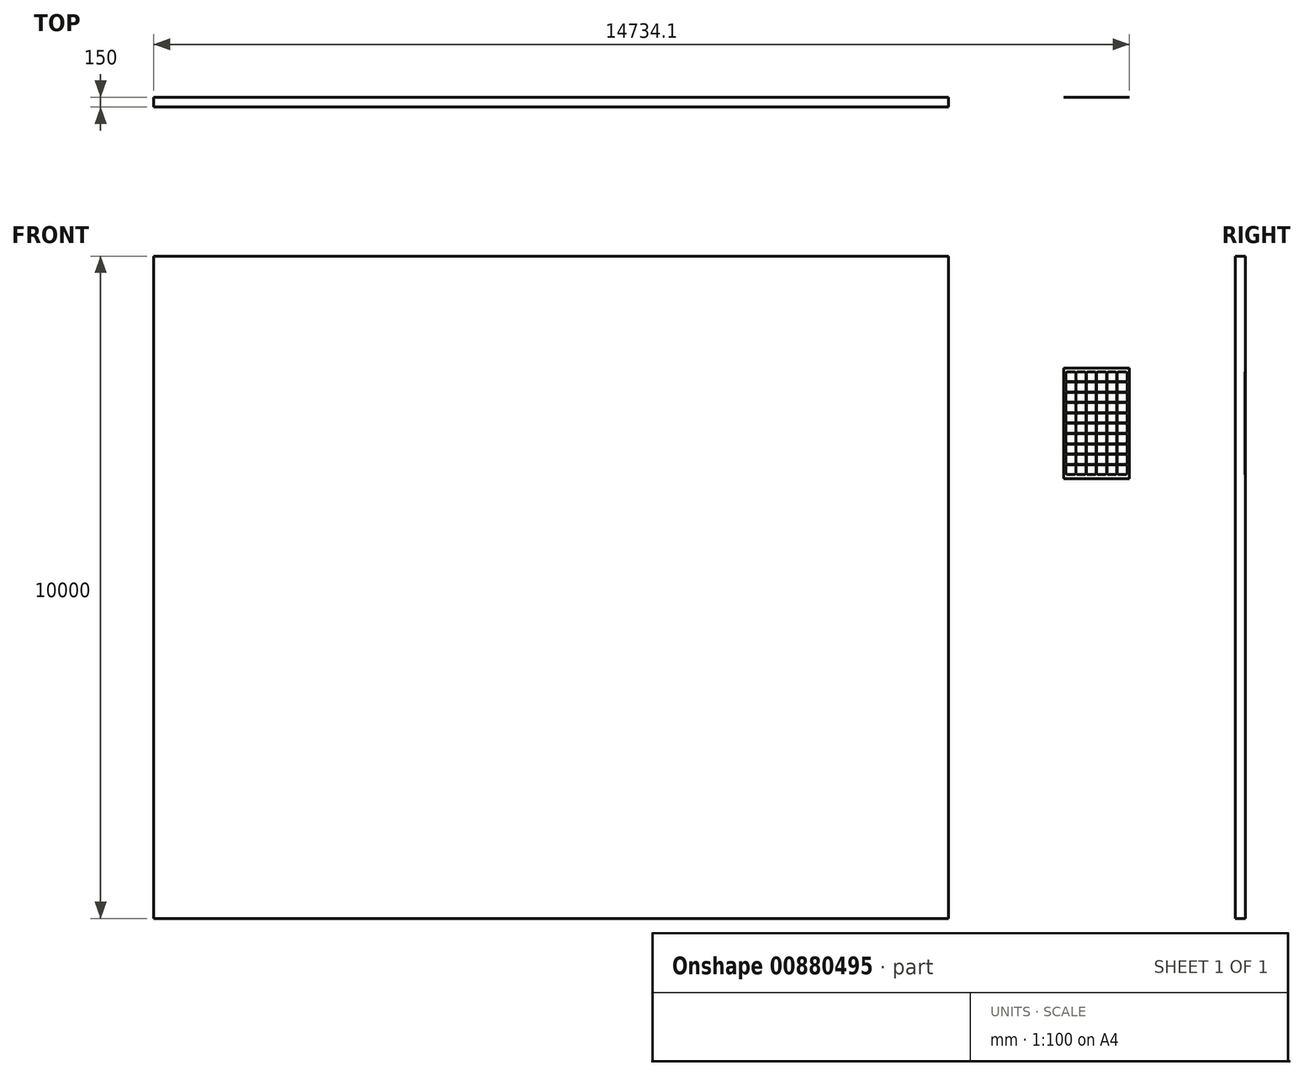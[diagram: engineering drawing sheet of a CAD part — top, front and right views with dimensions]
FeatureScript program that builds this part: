
annotation { "Feature Type Name" : "Feature", "Feature Type Description" : "" }
export const myFeature = defineFeature(function(context is Context, id is Id, definition is map)
    precondition{}
    {
        {
            var Q0;
            Q0=qCreatedBy(makeId("Front.planeOp"),FACE);
            var sketch = newSketch(context, id + "F0", { "sketchPlane" : qUnion([Q0])});
            skLineSegment(sketch, "E0.bottom", {"start": v(-6000, 5000) * mm, "end": v(6000, 5000) * mm});
            skLineSegment(sketch, "E0.top", {"start": v(-6000, -5000) * mm, "end": v(6000, -5000) * mm});
            skLineSegment(sketch, "E0.left", {"start": v(-6000, 5000) * mm, "end": v(-6000, -5000) * mm});
            skLineSegment(sketch, "E0.right", {"start": v(6000, 5000) * mm, "end": v(6000, -5000) * mm});
            skPoint(sketch, "E0.middle", {"position": v(0, 0) * mm});
            skSolve(sketch);
        }
        {
            var Q0;
            Q0=makeQuery(id+"F0.imprint","IMPRINT",FACE,{"disambiguationData":[TD([[makeQuery(id+"F0.imprint","IMPRINT",EDGE,{"derivedFrom":sQuery(id+"F0.wireOp",EDGE,"E0.bottom")}),-1.0]])]});
            var sketch = newSketch(context, id + "F1", { "sketchPlane" : qUnion([Q0])});
            skLineSegment(sketch, "E1.bottom", {"start": v(7744.06, 3311.69) * mm, "end": v(8734.06, 3311.69) * mm});
            skLineSegment(sketch, "E1.top", {"start": v(7744.06, 1636.69) * mm, "end": v(8734.06, 1636.69) * mm});
            skLineSegment(sketch, "E1.left", {"start": v(7744.06, 3311.69) * mm, "end": v(7744.06, 1636.69) * mm});
            skLineSegment(sketch, "E1.right", {"start": v(8734.06, 3311.69) * mm, "end": v(8734.06, 1636.69) * mm});
            skSolve(sketch);
        }
        {
            var Q0;
            Q0=makeQuery(id+"F1.imprint","IMPRINT",FACE,{"disambiguationData":[TD([[makeQuery(id+"F1.imprint","IMPRINT",EDGE,{"derivedFrom":sQuery(id+"F1.wireOp",EDGE,"E1.bottom")}),-1.0]])]});
            var sketch = newSketch(context, id + "F2", { "sketchPlane" : qUnion([Q0])});
            skLineSegment(sketch, "E2.bottom", {"start": v(7804.13, 1851.23) * mm, "end": v(7894.13, 1851.23) * mm});
            skLineSegment(sketch, "E2.top", {"start": v(7804.13, 1701.23) * mm, "end": v(7894.13, 1701.23) * mm});
            skLineSegment(sketch, "E2.left", {"start": v(7774.13, 1821.23) * mm, "end": v(7774.13, 1731.23) * mm});
            skLineSegment(sketch, "E2.right", {"start": v(7924.13, 1821.23) * mm, "end": v(7924.13, 1731.23) * mm});
            skPoint(sketch, "E3.visualSharp", {"position": v(7924.13, 1851.23) * mm});
            skArc(sketch, "E3.filletArc", {"start": v(7924.13, 1821.23) * mm, "mid": v(7915.35, 1842.44) * mm, "end": v(7894.13, 1851.23) * mm});
            skPoint(sketch, "E4.visualSharp", {"position": v(7774.13, 1851.23) * mm});
            skArc(sketch, "E4.filletArc", {"start": v(7804.13, 1851.23) * mm, "mid": v(7782.92, 1842.44) * mm, "end": v(7774.13, 1821.23) * mm});
            skPoint(sketch, "E5.visualSharp", {"position": v(7774.13, 1701.23) * mm});
            skArc(sketch, "E5.filletArc", {"start": v(7774.13, 1731.23) * mm, "mid": v(7782.92, 1710.01) * mm, "end": v(7804.13, 1701.23) * mm});
            skPoint(sketch, "E6.visualSharp", {"position": v(7924.13, 1701.23) * mm});
            skArc(sketch, "E6.filletArc", {"start": v(7894.13, 1701.23) * mm, "mid": v(7915.35, 1710.01) * mm, "end": v(7924.13, 1731.23) * mm});
            skLineSegment(sketch, "E7.0.1.0", {"start": v(7804.13, 2007.23) * mm, "end": v(7894.13, 2007.23) * mm});
            skArc(sketch, "E7.0.1.1", {"start": v(7804.13, 2007.23) * mm, "mid": v(7782.92, 1998.44) * mm, "end": v(7774.13, 1977.23) * mm});
            skLineSegment(sketch, "E7.0.1.2", {"start": v(7774.13, 1977.23) * mm, "end": v(7774.13, 1887.23) * mm});
            skLineSegment(sketch, "E7.0.1.3", {"start": v(7804.13, 1857.23) * mm, "end": v(7894.13, 1857.23) * mm});
            skArc(sketch, "E7.0.1.4", {"start": v(7774.13, 1887.23) * mm, "mid": v(7782.92, 1866.01) * mm, "end": v(7804.13, 1857.23) * mm});
            skArc(sketch, "E7.0.1.5", {"start": v(7894.13, 1857.23) * mm, "mid": v(7915.35, 1866.01) * mm, "end": v(7924.13, 1887.23) * mm});
            skLineSegment(sketch, "E7.0.1.6", {"start": v(7924.13, 1977.23) * mm, "end": v(7924.13, 1887.23) * mm});
            skArc(sketch, "E7.0.1.7", {"start": v(7924.13, 1977.23) * mm, "mid": v(7915.35, 1998.44) * mm, "end": v(7894.13, 2007.23) * mm});
            skLineSegment(sketch, "E7.0.2.0", {"start": v(7804.13, 2163.23) * mm, "end": v(7894.13, 2163.23) * mm});
            skArc(sketch, "E7.0.2.1", {"start": v(7804.13, 2163.23) * mm, "mid": v(7782.92, 2154.44) * mm, "end": v(7774.13, 2133.23) * mm});
            skLineSegment(sketch, "E7.0.2.2", {"start": v(7774.13, 2133.23) * mm, "end": v(7774.13, 2043.23) * mm});
            skLineSegment(sketch, "E7.0.2.3", {"start": v(7804.13, 2013.23) * mm, "end": v(7894.13, 2013.23) * mm});
            skArc(sketch, "E7.0.2.4", {"start": v(7774.13, 2043.23) * mm, "mid": v(7782.92, 2022.01) * mm, "end": v(7804.13, 2013.23) * mm});
            skArc(sketch, "E7.0.2.5", {"start": v(7894.13, 2013.23) * mm, "mid": v(7915.35, 2022.01) * mm, "end": v(7924.13, 2043.23) * mm});
            skLineSegment(sketch, "E7.0.2.6", {"start": v(7924.13, 2133.23) * mm, "end": v(7924.13, 2043.23) * mm});
            skArc(sketch, "E7.0.2.7", {"start": v(7924.13, 2133.23) * mm, "mid": v(7915.35, 2154.44) * mm, "end": v(7894.13, 2163.23) * mm});
            skLineSegment(sketch, "E7.0.3.0", {"start": v(7804.13, 2319.23) * mm, "end": v(7894.13, 2319.23) * mm});
            skArc(sketch, "E7.0.3.1", {"start": v(7804.13, 2319.23) * mm, "mid": v(7782.92, 2310.44) * mm, "end": v(7774.13, 2289.23) * mm});
            skLineSegment(sketch, "E7.0.3.2", {"start": v(7774.13, 2289.23) * mm, "end": v(7774.13, 2199.23) * mm});
            skLineSegment(sketch, "E7.0.3.3", {"start": v(7804.13, 2169.23) * mm, "end": v(7894.13, 2169.23) * mm});
            skArc(sketch, "E7.0.3.4", {"start": v(7774.13, 2199.23) * mm, "mid": v(7782.92, 2178.01) * mm, "end": v(7804.13, 2169.23) * mm});
            skArc(sketch, "E7.0.3.5", {"start": v(7894.13, 2169.23) * mm, "mid": v(7915.35, 2178.01) * mm, "end": v(7924.13, 2199.23) * mm});
            skLineSegment(sketch, "E7.0.3.6", {"start": v(7924.13, 2289.23) * mm, "end": v(7924.13, 2199.23) * mm});
            skArc(sketch, "E7.0.3.7", {"start": v(7924.13, 2289.23) * mm, "mid": v(7915.35, 2310.44) * mm, "end": v(7894.13, 2319.23) * mm});
            skLineSegment(sketch, "E7.0.4.0", {"start": v(7804.13, 2475.23) * mm, "end": v(7894.13, 2475.23) * mm});
            skArc(sketch, "E7.0.4.1", {"start": v(7804.13, 2475.23) * mm, "mid": v(7782.92, 2466.44) * mm, "end": v(7774.13, 2445.23) * mm});
            skLineSegment(sketch, "E7.0.4.2", {"start": v(7774.13, 2445.23) * mm, "end": v(7774.13, 2355.23) * mm});
            skLineSegment(sketch, "E7.0.4.3", {"start": v(7804.13, 2325.23) * mm, "end": v(7894.13, 2325.23) * mm});
            skArc(sketch, "E7.0.4.4", {"start": v(7774.13, 2355.23) * mm, "mid": v(7782.92, 2334.01) * mm, "end": v(7804.13, 2325.23) * mm});
            skArc(sketch, "E7.0.4.5", {"start": v(7894.13, 2325.23) * mm, "mid": v(7915.35, 2334.01) * mm, "end": v(7924.13, 2355.23) * mm});
            skLineSegment(sketch, "E7.0.4.6", {"start": v(7924.13, 2445.23) * mm, "end": v(7924.13, 2355.23) * mm});
            skArc(sketch, "E7.0.4.7", {"start": v(7924.13, 2445.23) * mm, "mid": v(7915.35, 2466.44) * mm, "end": v(7894.13, 2475.23) * mm});
            skLineSegment(sketch, "E7.0.5.0", {"start": v(7804.13, 2631.23) * mm, "end": v(7894.13, 2631.23) * mm});
            skArc(sketch, "E7.0.5.1", {"start": v(7804.13, 2631.23) * mm, "mid": v(7782.92, 2622.44) * mm, "end": v(7774.13, 2601.23) * mm});
            skLineSegment(sketch, "E7.0.5.2", {"start": v(7774.13, 2601.23) * mm, "end": v(7774.13, 2511.23) * mm});
            skLineSegment(sketch, "E7.0.5.3", {"start": v(7804.13, 2481.23) * mm, "end": v(7894.13, 2481.23) * mm});
            skArc(sketch, "E7.0.5.4", {"start": v(7774.13, 2511.23) * mm, "mid": v(7782.92, 2490.01) * mm, "end": v(7804.13, 2481.23) * mm});
            skArc(sketch, "E7.0.5.5", {"start": v(7894.13, 2481.23) * mm, "mid": v(7915.35, 2490.01) * mm, "end": v(7924.13, 2511.23) * mm});
            skLineSegment(sketch, "E7.0.5.6", {"start": v(7924.13, 2601.23) * mm, "end": v(7924.13, 2511.23) * mm});
            skArc(sketch, "E7.0.5.7", {"start": v(7924.13, 2601.23) * mm, "mid": v(7915.35, 2622.44) * mm, "end": v(7894.13, 2631.23) * mm});
            skLineSegment(sketch, "E7.0.6.0", {"start": v(7804.13, 2787.23) * mm, "end": v(7894.13, 2787.23) * mm});
            skArc(sketch, "E7.0.6.1", {"start": v(7804.13, 2787.23) * mm, "mid": v(7782.92, 2778.44) * mm, "end": v(7774.13, 2757.23) * mm});
            skLineSegment(sketch, "E7.0.6.2", {"start": v(7774.13, 2757.23) * mm, "end": v(7774.13, 2667.23) * mm});
            skLineSegment(sketch, "E7.0.6.3", {"start": v(7804.13, 2637.23) * mm, "end": v(7894.13, 2637.23) * mm});
            skArc(sketch, "E7.0.6.4", {"start": v(7774.13, 2667.23) * mm, "mid": v(7782.92, 2646.01) * mm, "end": v(7804.13, 2637.23) * mm});
            skArc(sketch, "E7.0.6.5", {"start": v(7894.13, 2637.23) * mm, "mid": v(7915.35, 2646.01) * mm, "end": v(7924.13, 2667.23) * mm});
            skLineSegment(sketch, "E7.0.6.6", {"start": v(7924.13, 2757.23) * mm, "end": v(7924.13, 2667.23) * mm});
            skArc(sketch, "E7.0.6.7", {"start": v(7924.13, 2757.23) * mm, "mid": v(7915.35, 2778.44) * mm, "end": v(7894.13, 2787.23) * mm});
            skLineSegment(sketch, "E7.0.7.0", {"start": v(7804.13, 2943.23) * mm, "end": v(7894.13, 2943.23) * mm});
            skArc(sketch, "E7.0.7.1", {"start": v(7804.13, 2943.23) * mm, "mid": v(7782.92, 2934.44) * mm, "end": v(7774.13, 2913.23) * mm});
            skLineSegment(sketch, "E7.0.7.2", {"start": v(7774.13, 2913.23) * mm, "end": v(7774.13, 2823.23) * mm});
            skLineSegment(sketch, "E7.0.7.3", {"start": v(7804.13, 2793.23) * mm, "end": v(7894.13, 2793.23) * mm});
            skArc(sketch, "E7.0.7.4", {"start": v(7774.13, 2823.23) * mm, "mid": v(7782.92, 2802.01) * mm, "end": v(7804.13, 2793.23) * mm});
            skArc(sketch, "E7.0.7.5", {"start": v(7894.13, 2793.23) * mm, "mid": v(7915.35, 2802.01) * mm, "end": v(7924.13, 2823.23) * mm});
            skLineSegment(sketch, "E7.0.7.6", {"start": v(7924.13, 2913.23) * mm, "end": v(7924.13, 2823.23) * mm});
            skArc(sketch, "E7.0.7.7", {"start": v(7924.13, 2913.23) * mm, "mid": v(7915.35, 2934.44) * mm, "end": v(7894.13, 2943.23) * mm});
            skLineSegment(sketch, "E7.0.8.0", {"start": v(7804.13, 3099.23) * mm, "end": v(7894.13, 3099.23) * mm});
            skArc(sketch, "E7.0.8.1", {"start": v(7804.13, 3099.23) * mm, "mid": v(7782.92, 3090.44) * mm, "end": v(7774.13, 3069.23) * mm});
            skLineSegment(sketch, "E7.0.8.2", {"start": v(7774.13, 3069.23) * mm, "end": v(7774.13, 2979.23) * mm});
            skLineSegment(sketch, "E7.0.8.3", {"start": v(7804.13, 2949.23) * mm, "end": v(7894.13, 2949.23) * mm});
            skArc(sketch, "E7.0.8.4", {"start": v(7774.13, 2979.23) * mm, "mid": v(7782.92, 2958.01) * mm, "end": v(7804.13, 2949.23) * mm});
            skArc(sketch, "E7.0.8.5", {"start": v(7894.13, 2949.23) * mm, "mid": v(7915.35, 2958.01) * mm, "end": v(7924.13, 2979.23) * mm});
            skLineSegment(sketch, "E7.0.8.6", {"start": v(7924.13, 3069.23) * mm, "end": v(7924.13, 2979.23) * mm});
            skArc(sketch, "E7.0.8.7", {"start": v(7924.13, 3069.23) * mm, "mid": v(7915.35, 3090.44) * mm, "end": v(7894.13, 3099.23) * mm});
            skLineSegment(sketch, "E7.0.9.0", {"start": v(7804.13, 3255.23) * mm, "end": v(7894.13, 3255.23) * mm});
            skArc(sketch, "E7.0.9.1", {"start": v(7804.13, 3255.23) * mm, "mid": v(7782.92, 3246.44) * mm, "end": v(7774.13, 3225.23) * mm});
            skLineSegment(sketch, "E7.0.9.2", {"start": v(7774.13, 3225.23) * mm, "end": v(7774.13, 3135.23) * mm});
            skLineSegment(sketch, "E7.0.9.3", {"start": v(7804.13, 3105.23) * mm, "end": v(7894.13, 3105.23) * mm});
            skArc(sketch, "E7.0.9.4", {"start": v(7774.13, 3135.23) * mm, "mid": v(7782.92, 3114.01) * mm, "end": v(7804.13, 3105.23) * mm});
            skArc(sketch, "E7.0.9.5", {"start": v(7894.13, 3105.23) * mm, "mid": v(7915.35, 3114.01) * mm, "end": v(7924.13, 3135.23) * mm});
            skLineSegment(sketch, "E7.0.9.6", {"start": v(7924.13, 3225.23) * mm, "end": v(7924.13, 3135.23) * mm});
            skArc(sketch, "E7.0.9.7", {"start": v(7924.13, 3225.23) * mm, "mid": v(7915.35, 3246.44) * mm, "end": v(7894.13, 3255.23) * mm});
            skLineSegment(sketch, "E7.1.0.0", {"start": v(7959.13, 1851.23) * mm, "end": v(8049.13, 1851.23) * mm});
            skArc(sketch, "E7.1.0.1", {"start": v(7959.13, 1851.23) * mm, "mid": v(7937.92, 1842.44) * mm, "end": v(7929.13, 1821.23) * mm});
            skLineSegment(sketch, "E7.1.0.2", {"start": v(7929.13, 1821.23) * mm, "end": v(7929.13, 1731.23) * mm});
            skLineSegment(sketch, "E7.1.0.3", {"start": v(7959.13, 1701.23) * mm, "end": v(8049.13, 1701.23) * mm});
            skArc(sketch, "E7.1.0.4", {"start": v(7929.13, 1731.23) * mm, "mid": v(7937.92, 1710.01) * mm, "end": v(7959.13, 1701.23) * mm});
            skArc(sketch, "E7.1.0.5", {"start": v(8049.13, 1701.23) * mm, "mid": v(8070.35, 1710.01) * mm, "end": v(8079.13, 1731.23) * mm});
            skLineSegment(sketch, "E7.1.0.6", {"start": v(8079.13, 1821.23) * mm, "end": v(8079.13, 1731.23) * mm});
            skArc(sketch, "E7.1.0.7", {"start": v(8079.13, 1821.23) * mm, "mid": v(8070.35, 1842.44) * mm, "end": v(8049.13, 1851.23) * mm});
            skLineSegment(sketch, "E7.1.1.0", {"start": v(7959.13, 2007.23) * mm, "end": v(8049.13, 2007.23) * mm});
            skArc(sketch, "E7.1.1.1", {"start": v(7959.13, 2007.23) * mm, "mid": v(7937.92, 1998.44) * mm, "end": v(7929.13, 1977.23) * mm});
            skLineSegment(sketch, "E7.1.1.2", {"start": v(7929.13, 1977.23) * mm, "end": v(7929.13, 1887.23) * mm});
            skLineSegment(sketch, "E7.1.1.3", {"start": v(7959.13, 1857.23) * mm, "end": v(8049.13, 1857.23) * mm});
            skArc(sketch, "E7.1.1.4", {"start": v(7929.13, 1887.23) * mm, "mid": v(7937.92, 1866.01) * mm, "end": v(7959.13, 1857.23) * mm});
            skArc(sketch, "E7.1.1.5", {"start": v(8049.13, 1857.23) * mm, "mid": v(8070.35, 1866.01) * mm, "end": v(8079.13, 1887.23) * mm});
            skLineSegment(sketch, "E7.1.1.6", {"start": v(8079.13, 1977.23) * mm, "end": v(8079.13, 1887.23) * mm});
            skArc(sketch, "E7.1.1.7", {"start": v(8079.13, 1977.23) * mm, "mid": v(8070.35, 1998.44) * mm, "end": v(8049.13, 2007.23) * mm});
            skLineSegment(sketch, "E7.1.2.0", {"start": v(7959.13, 2163.23) * mm, "end": v(8049.13, 2163.23) * mm});
            skArc(sketch, "E7.1.2.1", {"start": v(7959.13, 2163.23) * mm, "mid": v(7937.92, 2154.44) * mm, "end": v(7929.13, 2133.23) * mm});
            skLineSegment(sketch, "E7.1.2.2", {"start": v(7929.13, 2133.23) * mm, "end": v(7929.13, 2043.23) * mm});
            skLineSegment(sketch, "E7.1.2.3", {"start": v(7959.13, 2013.23) * mm, "end": v(8049.13, 2013.23) * mm});
            skArc(sketch, "E7.1.2.4", {"start": v(7929.13, 2043.23) * mm, "mid": v(7937.92, 2022.01) * mm, "end": v(7959.13, 2013.23) * mm});
            skArc(sketch, "E7.1.2.5", {"start": v(8049.13, 2013.23) * mm, "mid": v(8070.35, 2022.01) * mm, "end": v(8079.13, 2043.23) * mm});
            skLineSegment(sketch, "E7.1.2.6", {"start": v(8079.13, 2133.23) * mm, "end": v(8079.13, 2043.23) * mm});
            skArc(sketch, "E7.1.2.7", {"start": v(8079.13, 2133.23) * mm, "mid": v(8070.35, 2154.44) * mm, "end": v(8049.13, 2163.23) * mm});
            skLineSegment(sketch, "E7.1.3.0", {"start": v(7959.13, 2319.23) * mm, "end": v(8049.13, 2319.23) * mm});
            skArc(sketch, "E7.1.3.1", {"start": v(7959.13, 2319.23) * mm, "mid": v(7937.92, 2310.44) * mm, "end": v(7929.13, 2289.23) * mm});
            skLineSegment(sketch, "E7.1.3.2", {"start": v(7929.13, 2289.23) * mm, "end": v(7929.13, 2199.23) * mm});
            skLineSegment(sketch, "E7.1.3.3", {"start": v(7959.13, 2169.23) * mm, "end": v(8049.13, 2169.23) * mm});
            skArc(sketch, "E7.1.3.4", {"start": v(7929.13, 2199.23) * mm, "mid": v(7937.92, 2178.01) * mm, "end": v(7959.13, 2169.23) * mm});
            skArc(sketch, "E7.1.3.5", {"start": v(8049.13, 2169.23) * mm, "mid": v(8070.35, 2178.01) * mm, "end": v(8079.13, 2199.23) * mm});
            skLineSegment(sketch, "E7.1.3.6", {"start": v(8079.13, 2289.23) * mm, "end": v(8079.13, 2199.23) * mm});
            skArc(sketch, "E7.1.3.7", {"start": v(8079.13, 2289.23) * mm, "mid": v(8070.35, 2310.44) * mm, "end": v(8049.13, 2319.23) * mm});
            skLineSegment(sketch, "E7.1.4.0", {"start": v(7959.13, 2475.23) * mm, "end": v(8049.13, 2475.23) * mm});
            skArc(sketch, "E7.1.4.1", {"start": v(7959.13, 2475.23) * mm, "mid": v(7937.92, 2466.44) * mm, "end": v(7929.13, 2445.23) * mm});
            skLineSegment(sketch, "E7.1.4.2", {"start": v(7929.13, 2445.23) * mm, "end": v(7929.13, 2355.23) * mm});
            skLineSegment(sketch, "E7.1.4.3", {"start": v(7959.13, 2325.23) * mm, "end": v(8049.13, 2325.23) * mm});
            skArc(sketch, "E7.1.4.4", {"start": v(7929.13, 2355.23) * mm, "mid": v(7937.92, 2334.01) * mm, "end": v(7959.13, 2325.23) * mm});
            skArc(sketch, "E7.1.4.5", {"start": v(8049.13, 2325.23) * mm, "mid": v(8070.35, 2334.01) * mm, "end": v(8079.13, 2355.23) * mm});
            skLineSegment(sketch, "E7.1.4.6", {"start": v(8079.13, 2445.23) * mm, "end": v(8079.13, 2355.23) * mm});
            skArc(sketch, "E7.1.4.7", {"start": v(8079.13, 2445.23) * mm, "mid": v(8070.35, 2466.44) * mm, "end": v(8049.13, 2475.23) * mm});
            skLineSegment(sketch, "E7.1.5.0", {"start": v(7959.13, 2631.23) * mm, "end": v(8049.13, 2631.23) * mm});
            skArc(sketch, "E7.1.5.1", {"start": v(7959.13, 2631.23) * mm, "mid": v(7937.92, 2622.44) * mm, "end": v(7929.13, 2601.23) * mm});
            skLineSegment(sketch, "E7.1.5.2", {"start": v(7929.13, 2601.23) * mm, "end": v(7929.13, 2511.23) * mm});
            skLineSegment(sketch, "E7.1.5.3", {"start": v(7959.13, 2481.23) * mm, "end": v(8049.13, 2481.23) * mm});
            skArc(sketch, "E7.1.5.4", {"start": v(7929.13, 2511.23) * mm, "mid": v(7937.92, 2490.01) * mm, "end": v(7959.13, 2481.23) * mm});
            skArc(sketch, "E7.1.5.5", {"start": v(8049.13, 2481.23) * mm, "mid": v(8070.35, 2490.01) * mm, "end": v(8079.13, 2511.23) * mm});
            skLineSegment(sketch, "E7.1.5.6", {"start": v(8079.13, 2601.23) * mm, "end": v(8079.13, 2511.23) * mm});
            skArc(sketch, "E7.1.5.7", {"start": v(8079.13, 2601.23) * mm, "mid": v(8070.35, 2622.44) * mm, "end": v(8049.13, 2631.23) * mm});
            skLineSegment(sketch, "E7.1.6.0", {"start": v(7959.13, 2787.23) * mm, "end": v(8049.13, 2787.23) * mm});
            skArc(sketch, "E7.1.6.1", {"start": v(7959.13, 2787.23) * mm, "mid": v(7937.92, 2778.44) * mm, "end": v(7929.13, 2757.23) * mm});
            skLineSegment(sketch, "E7.1.6.2", {"start": v(7929.13, 2757.23) * mm, "end": v(7929.13, 2667.23) * mm});
            skLineSegment(sketch, "E7.1.6.3", {"start": v(7959.13, 2637.23) * mm, "end": v(8049.13, 2637.23) * mm});
            skArc(sketch, "E7.1.6.4", {"start": v(7929.13, 2667.23) * mm, "mid": v(7937.92, 2646.01) * mm, "end": v(7959.13, 2637.23) * mm});
            skArc(sketch, "E7.1.6.5", {"start": v(8049.13, 2637.23) * mm, "mid": v(8070.35, 2646.01) * mm, "end": v(8079.13, 2667.23) * mm});
            skLineSegment(sketch, "E7.1.6.6", {"start": v(8079.13, 2757.23) * mm, "end": v(8079.13, 2667.23) * mm});
            skArc(sketch, "E7.1.6.7", {"start": v(8079.13, 2757.23) * mm, "mid": v(8070.35, 2778.44) * mm, "end": v(8049.13, 2787.23) * mm});
            skLineSegment(sketch, "E7.1.7.0", {"start": v(7959.13, 2943.23) * mm, "end": v(8049.13, 2943.23) * mm});
            skArc(sketch, "E7.1.7.1", {"start": v(7959.13, 2943.23) * mm, "mid": v(7937.92, 2934.44) * mm, "end": v(7929.13, 2913.23) * mm});
            skLineSegment(sketch, "E7.1.7.2", {"start": v(7929.13, 2913.23) * mm, "end": v(7929.13, 2823.23) * mm});
            skLineSegment(sketch, "E7.1.7.3", {"start": v(7959.13, 2793.23) * mm, "end": v(8049.13, 2793.23) * mm});
            skArc(sketch, "E7.1.7.4", {"start": v(7929.13, 2823.23) * mm, "mid": v(7937.92, 2802.01) * mm, "end": v(7959.13, 2793.23) * mm});
            skArc(sketch, "E7.1.7.5", {"start": v(8049.13, 2793.23) * mm, "mid": v(8070.35, 2802.01) * mm, "end": v(8079.13, 2823.23) * mm});
            skLineSegment(sketch, "E7.1.7.6", {"start": v(8079.13, 2913.23) * mm, "end": v(8079.13, 2823.23) * mm});
            skArc(sketch, "E7.1.7.7", {"start": v(8079.13, 2913.23) * mm, "mid": v(8070.35, 2934.44) * mm, "end": v(8049.13, 2943.23) * mm});
            skLineSegment(sketch, "E7.1.8.0", {"start": v(7959.13, 3099.23) * mm, "end": v(8049.13, 3099.23) * mm});
            skArc(sketch, "E7.1.8.1", {"start": v(7959.13, 3099.23) * mm, "mid": v(7937.92, 3090.44) * mm, "end": v(7929.13, 3069.23) * mm});
            skLineSegment(sketch, "E7.1.8.2", {"start": v(7929.13, 3069.23) * mm, "end": v(7929.13, 2979.23) * mm});
            skLineSegment(sketch, "E7.1.8.3", {"start": v(7959.13, 2949.23) * mm, "end": v(8049.13, 2949.23) * mm});
            skArc(sketch, "E7.1.8.4", {"start": v(7929.13, 2979.23) * mm, "mid": v(7937.92, 2958.01) * mm, "end": v(7959.13, 2949.23) * mm});
            skArc(sketch, "E7.1.8.5", {"start": v(8049.13, 2949.23) * mm, "mid": v(8070.35, 2958.01) * mm, "end": v(8079.13, 2979.23) * mm});
            skLineSegment(sketch, "E7.1.8.6", {"start": v(8079.13, 3069.23) * mm, "end": v(8079.13, 2979.23) * mm});
            skArc(sketch, "E7.1.8.7", {"start": v(8079.13, 3069.23) * mm, "mid": v(8070.35, 3090.44) * mm, "end": v(8049.13, 3099.23) * mm});
            skLineSegment(sketch, "E7.1.9.0", {"start": v(7959.13, 3255.23) * mm, "end": v(8049.13, 3255.23) * mm});
            skArc(sketch, "E7.1.9.1", {"start": v(7959.13, 3255.23) * mm, "mid": v(7937.92, 3246.44) * mm, "end": v(7929.13, 3225.23) * mm});
            skLineSegment(sketch, "E7.1.9.2", {"start": v(7929.13, 3225.23) * mm, "end": v(7929.13, 3135.23) * mm});
            skLineSegment(sketch, "E7.1.9.3", {"start": v(7959.13, 3105.23) * mm, "end": v(8049.13, 3105.23) * mm});
            skArc(sketch, "E7.1.9.4", {"start": v(7929.13, 3135.23) * mm, "mid": v(7937.92, 3114.01) * mm, "end": v(7959.13, 3105.23) * mm});
            skArc(sketch, "E7.1.9.5", {"start": v(8049.13, 3105.23) * mm, "mid": v(8070.35, 3114.01) * mm, "end": v(8079.13, 3135.23) * mm});
            skLineSegment(sketch, "E7.1.9.6", {"start": v(8079.13, 3225.23) * mm, "end": v(8079.13, 3135.23) * mm});
            skArc(sketch, "E7.1.9.7", {"start": v(8079.13, 3225.23) * mm, "mid": v(8070.35, 3246.44) * mm, "end": v(8049.13, 3255.23) * mm});
            skLineSegment(sketch, "E7.2.0.0", {"start": v(8114.13, 1851.23) * mm, "end": v(8204.13, 1851.23) * mm});
            skArc(sketch, "E7.2.0.1", {"start": v(8114.13, 1851.23) * mm, "mid": v(8092.92, 1842.44) * mm, "end": v(8084.13, 1821.23) * mm});
            skLineSegment(sketch, "E7.2.0.2", {"start": v(8084.13, 1821.23) * mm, "end": v(8084.13, 1731.23) * mm});
            skLineSegment(sketch, "E7.2.0.3", {"start": v(8114.13, 1701.23) * mm, "end": v(8204.13, 1701.23) * mm});
            skArc(sketch, "E7.2.0.4", {"start": v(8084.13, 1731.23) * mm, "mid": v(8092.92, 1710.01) * mm, "end": v(8114.13, 1701.23) * mm});
            skArc(sketch, "E7.2.0.5", {"start": v(8204.13, 1701.23) * mm, "mid": v(8225.35, 1710.01) * mm, "end": v(8234.13, 1731.23) * mm});
            skLineSegment(sketch, "E7.2.0.6", {"start": v(8234.13, 1821.23) * mm, "end": v(8234.13, 1731.23) * mm});
            skArc(sketch, "E7.2.0.7", {"start": v(8234.13, 1821.23) * mm, "mid": v(8225.35, 1842.44) * mm, "end": v(8204.13, 1851.23) * mm});
            skLineSegment(sketch, "E7.2.1.0", {"start": v(8114.13, 2007.23) * mm, "end": v(8204.13, 2007.23) * mm});
            skArc(sketch, "E7.2.1.1", {"start": v(8114.13, 2007.23) * mm, "mid": v(8092.92, 1998.44) * mm, "end": v(8084.13, 1977.23) * mm});
            skLineSegment(sketch, "E7.2.1.2", {"start": v(8084.13, 1977.23) * mm, "end": v(8084.13, 1887.23) * mm});
            skLineSegment(sketch, "E7.2.1.3", {"start": v(8114.13, 1857.23) * mm, "end": v(8204.13, 1857.23) * mm});
            skArc(sketch, "E7.2.1.4", {"start": v(8084.13, 1887.23) * mm, "mid": v(8092.92, 1866.01) * mm, "end": v(8114.13, 1857.23) * mm});
            skArc(sketch, "E7.2.1.5", {"start": v(8204.13, 1857.23) * mm, "mid": v(8225.35, 1866.01) * mm, "end": v(8234.13, 1887.23) * mm});
            skLineSegment(sketch, "E7.2.1.6", {"start": v(8234.13, 1977.23) * mm, "end": v(8234.13, 1887.23) * mm});
            skArc(sketch, "E7.2.1.7", {"start": v(8234.13, 1977.23) * mm, "mid": v(8225.35, 1998.44) * mm, "end": v(8204.13, 2007.23) * mm});
            skLineSegment(sketch, "E7.2.2.0", {"start": v(8114.13, 2163.23) * mm, "end": v(8204.13, 2163.23) * mm});
            skArc(sketch, "E7.2.2.1", {"start": v(8114.13, 2163.23) * mm, "mid": v(8092.92, 2154.44) * mm, "end": v(8084.13, 2133.23) * mm});
            skLineSegment(sketch, "E7.2.2.2", {"start": v(8084.13, 2133.23) * mm, "end": v(8084.13, 2043.23) * mm});
            skLineSegment(sketch, "E7.2.2.3", {"start": v(8114.13, 2013.23) * mm, "end": v(8204.13, 2013.23) * mm});
            skArc(sketch, "E7.2.2.4", {"start": v(8084.13, 2043.23) * mm, "mid": v(8092.92, 2022.01) * mm, "end": v(8114.13, 2013.23) * mm});
            skArc(sketch, "E7.2.2.5", {"start": v(8204.13, 2013.23) * mm, "mid": v(8225.35, 2022.01) * mm, "end": v(8234.13, 2043.23) * mm});
            skLineSegment(sketch, "E7.2.2.6", {"start": v(8234.13, 2133.23) * mm, "end": v(8234.13, 2043.23) * mm});
            skArc(sketch, "E7.2.2.7", {"start": v(8234.13, 2133.23) * mm, "mid": v(8225.35, 2154.44) * mm, "end": v(8204.13, 2163.23) * mm});
            skLineSegment(sketch, "E7.2.3.0", {"start": v(8114.13, 2319.23) * mm, "end": v(8204.13, 2319.23) * mm});
            skArc(sketch, "E7.2.3.1", {"start": v(8114.13, 2319.23) * mm, "mid": v(8092.92, 2310.44) * mm, "end": v(8084.13, 2289.23) * mm});
            skLineSegment(sketch, "E7.2.3.2", {"start": v(8084.13, 2289.23) * mm, "end": v(8084.13, 2199.23) * mm});
            skLineSegment(sketch, "E7.2.3.3", {"start": v(8114.13, 2169.23) * mm, "end": v(8204.13, 2169.23) * mm});
            skArc(sketch, "E7.2.3.4", {"start": v(8084.13, 2199.23) * mm, "mid": v(8092.92, 2178.01) * mm, "end": v(8114.13, 2169.23) * mm});
            skArc(sketch, "E7.2.3.5", {"start": v(8204.13, 2169.23) * mm, "mid": v(8225.35, 2178.01) * mm, "end": v(8234.13, 2199.23) * mm});
            skLineSegment(sketch, "E7.2.3.6", {"start": v(8234.13, 2289.23) * mm, "end": v(8234.13, 2199.23) * mm});
            skArc(sketch, "E7.2.3.7", {"start": v(8234.13, 2289.23) * mm, "mid": v(8225.35, 2310.44) * mm, "end": v(8204.13, 2319.23) * mm});
            skLineSegment(sketch, "E7.2.4.0", {"start": v(8114.13, 2475.23) * mm, "end": v(8204.13, 2475.23) * mm});
            skArc(sketch, "E7.2.4.1", {"start": v(8114.13, 2475.23) * mm, "mid": v(8092.92, 2466.44) * mm, "end": v(8084.13, 2445.23) * mm});
            skLineSegment(sketch, "E7.2.4.2", {"start": v(8084.13, 2445.23) * mm, "end": v(8084.13, 2355.23) * mm});
            skLineSegment(sketch, "E7.2.4.3", {"start": v(8114.13, 2325.23) * mm, "end": v(8204.13, 2325.23) * mm});
            skArc(sketch, "E7.2.4.4", {"start": v(8084.13, 2355.23) * mm, "mid": v(8092.92, 2334.01) * mm, "end": v(8114.13, 2325.23) * mm});
            skArc(sketch, "E7.2.4.5", {"start": v(8204.13, 2325.23) * mm, "mid": v(8225.35, 2334.01) * mm, "end": v(8234.13, 2355.23) * mm});
            skLineSegment(sketch, "E7.2.4.6", {"start": v(8234.13, 2445.23) * mm, "end": v(8234.13, 2355.23) * mm});
            skArc(sketch, "E7.2.4.7", {"start": v(8234.13, 2445.23) * mm, "mid": v(8225.35, 2466.44) * mm, "end": v(8204.13, 2475.23) * mm});
            skLineSegment(sketch, "E7.2.5.0", {"start": v(8114.13, 2631.23) * mm, "end": v(8204.13, 2631.23) * mm});
            skArc(sketch, "E7.2.5.1", {"start": v(8114.13, 2631.23) * mm, "mid": v(8092.92, 2622.44) * mm, "end": v(8084.13, 2601.23) * mm});
            skLineSegment(sketch, "E7.2.5.2", {"start": v(8084.13, 2601.23) * mm, "end": v(8084.13, 2511.23) * mm});
            skLineSegment(sketch, "E7.2.5.3", {"start": v(8114.13, 2481.23) * mm, "end": v(8204.13, 2481.23) * mm});
            skArc(sketch, "E7.2.5.4", {"start": v(8084.13, 2511.23) * mm, "mid": v(8092.92, 2490.01) * mm, "end": v(8114.13, 2481.23) * mm});
            skArc(sketch, "E7.2.5.5", {"start": v(8204.13, 2481.23) * mm, "mid": v(8225.35, 2490.01) * mm, "end": v(8234.13, 2511.23) * mm});
            skLineSegment(sketch, "E7.2.5.6", {"start": v(8234.13, 2601.23) * mm, "end": v(8234.13, 2511.23) * mm});
            skArc(sketch, "E7.2.5.7", {"start": v(8234.13, 2601.23) * mm, "mid": v(8225.35, 2622.44) * mm, "end": v(8204.13, 2631.23) * mm});
            skLineSegment(sketch, "E7.2.6.0", {"start": v(8114.13, 2787.23) * mm, "end": v(8204.13, 2787.23) * mm});
            skArc(sketch, "E7.2.6.1", {"start": v(8114.13, 2787.23) * mm, "mid": v(8092.92, 2778.44) * mm, "end": v(8084.13, 2757.23) * mm});
            skLineSegment(sketch, "E7.2.6.2", {"start": v(8084.13, 2757.23) * mm, "end": v(8084.13, 2667.23) * mm});
            skLineSegment(sketch, "E7.2.6.3", {"start": v(8114.13, 2637.23) * mm, "end": v(8204.13, 2637.23) * mm});
            skArc(sketch, "E7.2.6.4", {"start": v(8084.13, 2667.23) * mm, "mid": v(8092.92, 2646.01) * mm, "end": v(8114.13, 2637.23) * mm});
            skArc(sketch, "E7.2.6.5", {"start": v(8204.13, 2637.23) * mm, "mid": v(8225.35, 2646.01) * mm, "end": v(8234.13, 2667.23) * mm});
            skLineSegment(sketch, "E7.2.6.6", {"start": v(8234.13, 2757.23) * mm, "end": v(8234.13, 2667.23) * mm});
            skArc(sketch, "E7.2.6.7", {"start": v(8234.13, 2757.23) * mm, "mid": v(8225.35, 2778.44) * mm, "end": v(8204.13, 2787.23) * mm});
            skLineSegment(sketch, "E7.2.7.0", {"start": v(8114.13, 2943.23) * mm, "end": v(8204.13, 2943.23) * mm});
            skArc(sketch, "E7.2.7.1", {"start": v(8114.13, 2943.23) * mm, "mid": v(8092.92, 2934.44) * mm, "end": v(8084.13, 2913.23) * mm});
            skLineSegment(sketch, "E7.2.7.2", {"start": v(8084.13, 2913.23) * mm, "end": v(8084.13, 2823.23) * mm});
            skLineSegment(sketch, "E7.2.7.3", {"start": v(8114.13, 2793.23) * mm, "end": v(8204.13, 2793.23) * mm});
            skArc(sketch, "E7.2.7.4", {"start": v(8084.13, 2823.23) * mm, "mid": v(8092.92, 2802.01) * mm, "end": v(8114.13, 2793.23) * mm});
            skArc(sketch, "E7.2.7.5", {"start": v(8204.13, 2793.23) * mm, "mid": v(8225.35, 2802.01) * mm, "end": v(8234.13, 2823.23) * mm});
            skLineSegment(sketch, "E7.2.7.6", {"start": v(8234.13, 2913.23) * mm, "end": v(8234.13, 2823.23) * mm});
            skArc(sketch, "E7.2.7.7", {"start": v(8234.13, 2913.23) * mm, "mid": v(8225.35, 2934.44) * mm, "end": v(8204.13, 2943.23) * mm});
            skLineSegment(sketch, "E7.2.8.0", {"start": v(8114.13, 3099.23) * mm, "end": v(8204.13, 3099.23) * mm});
            skArc(sketch, "E7.2.8.1", {"start": v(8114.13, 3099.23) * mm, "mid": v(8092.92, 3090.44) * mm, "end": v(8084.13, 3069.23) * mm});
            skLineSegment(sketch, "E7.2.8.2", {"start": v(8084.13, 3069.23) * mm, "end": v(8084.13, 2979.23) * mm});
            skLineSegment(sketch, "E7.2.8.3", {"start": v(8114.13, 2949.23) * mm, "end": v(8204.13, 2949.23) * mm});
            skArc(sketch, "E7.2.8.4", {"start": v(8084.13, 2979.23) * mm, "mid": v(8092.92, 2958.01) * mm, "end": v(8114.13, 2949.23) * mm});
            skArc(sketch, "E7.2.8.5", {"start": v(8204.13, 2949.23) * mm, "mid": v(8225.35, 2958.01) * mm, "end": v(8234.13, 2979.23) * mm});
            skLineSegment(sketch, "E7.2.8.6", {"start": v(8234.13, 3069.23) * mm, "end": v(8234.13, 2979.23) * mm});
            skArc(sketch, "E7.2.8.7", {"start": v(8234.13, 3069.23) * mm, "mid": v(8225.35, 3090.44) * mm, "end": v(8204.13, 3099.23) * mm});
            skLineSegment(sketch, "E7.2.9.0", {"start": v(8114.13, 3255.23) * mm, "end": v(8204.13, 3255.23) * mm});
            skArc(sketch, "E7.2.9.1", {"start": v(8114.13, 3255.23) * mm, "mid": v(8092.92, 3246.44) * mm, "end": v(8084.13, 3225.23) * mm});
            skLineSegment(sketch, "E7.2.9.2", {"start": v(8084.13, 3225.23) * mm, "end": v(8084.13, 3135.23) * mm});
            skLineSegment(sketch, "E7.2.9.3", {"start": v(8114.13, 3105.23) * mm, "end": v(8204.13, 3105.23) * mm});
            skArc(sketch, "E7.2.9.4", {"start": v(8084.13, 3135.23) * mm, "mid": v(8092.92, 3114.01) * mm, "end": v(8114.13, 3105.23) * mm});
            skArc(sketch, "E7.2.9.5", {"start": v(8204.13, 3105.23) * mm, "mid": v(8225.35, 3114.01) * mm, "end": v(8234.13, 3135.23) * mm});
            skLineSegment(sketch, "E7.2.9.6", {"start": v(8234.13, 3225.23) * mm, "end": v(8234.13, 3135.23) * mm});
            skArc(sketch, "E7.2.9.7", {"start": v(8234.13, 3225.23) * mm, "mid": v(8225.35, 3246.44) * mm, "end": v(8204.13, 3255.23) * mm});
            skLineSegment(sketch, "E7.3.0.0", {"start": v(8269.13, 1851.23) * mm, "end": v(8359.13, 1851.23) * mm});
            skArc(sketch, "E7.3.0.1", {"start": v(8269.13, 1851.23) * mm, "mid": v(8247.92, 1842.44) * mm, "end": v(8239.13, 1821.23) * mm});
            skLineSegment(sketch, "E7.3.0.2", {"start": v(8239.13, 1821.23) * mm, "end": v(8239.13, 1731.23) * mm});
            skLineSegment(sketch, "E7.3.0.3", {"start": v(8269.13, 1701.23) * mm, "end": v(8359.13, 1701.23) * mm});
            skArc(sketch, "E7.3.0.4", {"start": v(8239.13, 1731.23) * mm, "mid": v(8247.92, 1710.01) * mm, "end": v(8269.13, 1701.23) * mm});
            skArc(sketch, "E7.3.0.5", {"start": v(8359.13, 1701.23) * mm, "mid": v(8380.35, 1710.01) * mm, "end": v(8389.13, 1731.23) * mm});
            skLineSegment(sketch, "E7.3.0.6", {"start": v(8389.13, 1821.23) * mm, "end": v(8389.13, 1731.23) * mm});
            skArc(sketch, "E7.3.0.7", {"start": v(8389.13, 1821.23) * mm, "mid": v(8380.35, 1842.44) * mm, "end": v(8359.13, 1851.23) * mm});
            skLineSegment(sketch, "E7.3.1.0", {"start": v(8269.13, 2007.23) * mm, "end": v(8359.13, 2007.23) * mm});
            skArc(sketch, "E7.3.1.1", {"start": v(8269.13, 2007.23) * mm, "mid": v(8247.92, 1998.44) * mm, "end": v(8239.13, 1977.23) * mm});
            skLineSegment(sketch, "E7.3.1.2", {"start": v(8239.13, 1977.23) * mm, "end": v(8239.13, 1887.23) * mm});
            skLineSegment(sketch, "E7.3.1.3", {"start": v(8269.13, 1857.23) * mm, "end": v(8359.13, 1857.23) * mm});
            skArc(sketch, "E7.3.1.4", {"start": v(8239.13, 1887.23) * mm, "mid": v(8247.92, 1866.01) * mm, "end": v(8269.13, 1857.23) * mm});
            skArc(sketch, "E7.3.1.5", {"start": v(8359.13, 1857.23) * mm, "mid": v(8380.35, 1866.01) * mm, "end": v(8389.13, 1887.23) * mm});
            skLineSegment(sketch, "E7.3.1.6", {"start": v(8389.13, 1977.23) * mm, "end": v(8389.13, 1887.23) * mm});
            skArc(sketch, "E7.3.1.7", {"start": v(8389.13, 1977.23) * mm, "mid": v(8380.35, 1998.44) * mm, "end": v(8359.13, 2007.23) * mm});
            skLineSegment(sketch, "E7.3.2.0", {"start": v(8269.13, 2163.23) * mm, "end": v(8359.13, 2163.23) * mm});
            skArc(sketch, "E7.3.2.1", {"start": v(8269.13, 2163.23) * mm, "mid": v(8247.92, 2154.44) * mm, "end": v(8239.13, 2133.23) * mm});
            skLineSegment(sketch, "E7.3.2.2", {"start": v(8239.13, 2133.23) * mm, "end": v(8239.13, 2043.23) * mm});
            skLineSegment(sketch, "E7.3.2.3", {"start": v(8269.13, 2013.23) * mm, "end": v(8359.13, 2013.23) * mm});
            skArc(sketch, "E7.3.2.4", {"start": v(8239.13, 2043.23) * mm, "mid": v(8247.92, 2022.01) * mm, "end": v(8269.13, 2013.23) * mm});
            skArc(sketch, "E7.3.2.5", {"start": v(8359.13, 2013.23) * mm, "mid": v(8380.35, 2022.01) * mm, "end": v(8389.13, 2043.23) * mm});
            skLineSegment(sketch, "E7.3.2.6", {"start": v(8389.13, 2133.23) * mm, "end": v(8389.13, 2043.23) * mm});
            skArc(sketch, "E7.3.2.7", {"start": v(8389.13, 2133.23) * mm, "mid": v(8380.35, 2154.44) * mm, "end": v(8359.13, 2163.23) * mm});
            skLineSegment(sketch, "E7.3.3.0", {"start": v(8269.13, 2319.23) * mm, "end": v(8359.13, 2319.23) * mm});
            skArc(sketch, "E7.3.3.1", {"start": v(8269.13, 2319.23) * mm, "mid": v(8247.92, 2310.44) * mm, "end": v(8239.13, 2289.23) * mm});
            skLineSegment(sketch, "E7.3.3.2", {"start": v(8239.13, 2289.23) * mm, "end": v(8239.13, 2199.23) * mm});
            skLineSegment(sketch, "E7.3.3.3", {"start": v(8269.13, 2169.23) * mm, "end": v(8359.13, 2169.23) * mm});
            skArc(sketch, "E7.3.3.4", {"start": v(8239.13, 2199.23) * mm, "mid": v(8247.92, 2178.01) * mm, "end": v(8269.13, 2169.23) * mm});
            skArc(sketch, "E7.3.3.5", {"start": v(8359.13, 2169.23) * mm, "mid": v(8380.35, 2178.01) * mm, "end": v(8389.13, 2199.23) * mm});
            skLineSegment(sketch, "E7.3.3.6", {"start": v(8389.13, 2289.23) * mm, "end": v(8389.13, 2199.23) * mm});
            skArc(sketch, "E7.3.3.7", {"start": v(8389.13, 2289.23) * mm, "mid": v(8380.35, 2310.44) * mm, "end": v(8359.13, 2319.23) * mm});
            skLineSegment(sketch, "E7.3.4.0", {"start": v(8269.13, 2475.23) * mm, "end": v(8359.13, 2475.23) * mm});
            skArc(sketch, "E7.3.4.1", {"start": v(8269.13, 2475.23) * mm, "mid": v(8247.92, 2466.44) * mm, "end": v(8239.13, 2445.23) * mm});
            skLineSegment(sketch, "E7.3.4.2", {"start": v(8239.13, 2445.23) * mm, "end": v(8239.13, 2355.23) * mm});
            skLineSegment(sketch, "E7.3.4.3", {"start": v(8269.13, 2325.23) * mm, "end": v(8359.13, 2325.23) * mm});
            skArc(sketch, "E7.3.4.4", {"start": v(8239.13, 2355.23) * mm, "mid": v(8247.92, 2334.01) * mm, "end": v(8269.13, 2325.23) * mm});
            skArc(sketch, "E7.3.4.5", {"start": v(8359.13, 2325.23) * mm, "mid": v(8380.35, 2334.01) * mm, "end": v(8389.13, 2355.23) * mm});
            skLineSegment(sketch, "E7.3.4.6", {"start": v(8389.13, 2445.23) * mm, "end": v(8389.13, 2355.23) * mm});
            skArc(sketch, "E7.3.4.7", {"start": v(8389.13, 2445.23) * mm, "mid": v(8380.35, 2466.44) * mm, "end": v(8359.13, 2475.23) * mm});
            skLineSegment(sketch, "E7.3.5.0", {"start": v(8269.13, 2631.23) * mm, "end": v(8359.13, 2631.23) * mm});
            skArc(sketch, "E7.3.5.1", {"start": v(8269.13, 2631.23) * mm, "mid": v(8247.92, 2622.44) * mm, "end": v(8239.13, 2601.23) * mm});
            skLineSegment(sketch, "E7.3.5.2", {"start": v(8239.13, 2601.23) * mm, "end": v(8239.13, 2511.23) * mm});
            skLineSegment(sketch, "E7.3.5.3", {"start": v(8269.13, 2481.23) * mm, "end": v(8359.13, 2481.23) * mm});
            skArc(sketch, "E7.3.5.4", {"start": v(8239.13, 2511.23) * mm, "mid": v(8247.92, 2490.01) * mm, "end": v(8269.13, 2481.23) * mm});
            skArc(sketch, "E7.3.5.5", {"start": v(8359.13, 2481.23) * mm, "mid": v(8380.35, 2490.01) * mm, "end": v(8389.13, 2511.23) * mm});
            skLineSegment(sketch, "E7.3.5.6", {"start": v(8389.13, 2601.23) * mm, "end": v(8389.13, 2511.23) * mm});
            skArc(sketch, "E7.3.5.7", {"start": v(8389.13, 2601.23) * mm, "mid": v(8380.35, 2622.44) * mm, "end": v(8359.13, 2631.23) * mm});
            skLineSegment(sketch, "E7.3.6.0", {"start": v(8269.13, 2787.23) * mm, "end": v(8359.13, 2787.23) * mm});
            skArc(sketch, "E7.3.6.1", {"start": v(8269.13, 2787.23) * mm, "mid": v(8247.92, 2778.44) * mm, "end": v(8239.13, 2757.23) * mm});
            skLineSegment(sketch, "E7.3.6.2", {"start": v(8239.13, 2757.23) * mm, "end": v(8239.13, 2667.23) * mm});
            skLineSegment(sketch, "E7.3.6.3", {"start": v(8269.13, 2637.23) * mm, "end": v(8359.13, 2637.23) * mm});
            skArc(sketch, "E7.3.6.4", {"start": v(8239.13, 2667.23) * mm, "mid": v(8247.92, 2646.01) * mm, "end": v(8269.13, 2637.23) * mm});
            skArc(sketch, "E7.3.6.5", {"start": v(8359.13, 2637.23) * mm, "mid": v(8380.35, 2646.01) * mm, "end": v(8389.13, 2667.23) * mm});
            skLineSegment(sketch, "E7.3.6.6", {"start": v(8389.13, 2757.23) * mm, "end": v(8389.13, 2667.23) * mm});
            skArc(sketch, "E7.3.6.7", {"start": v(8389.13, 2757.23) * mm, "mid": v(8380.35, 2778.44) * mm, "end": v(8359.13, 2787.23) * mm});
            skLineSegment(sketch, "E7.3.7.0", {"start": v(8269.13, 2943.23) * mm, "end": v(8359.13, 2943.23) * mm});
            skArc(sketch, "E7.3.7.1", {"start": v(8269.13, 2943.23) * mm, "mid": v(8247.92, 2934.44) * mm, "end": v(8239.13, 2913.23) * mm});
            skLineSegment(sketch, "E7.3.7.2", {"start": v(8239.13, 2913.23) * mm, "end": v(8239.13, 2823.23) * mm});
            skLineSegment(sketch, "E7.3.7.3", {"start": v(8269.13, 2793.23) * mm, "end": v(8359.13, 2793.23) * mm});
            skArc(sketch, "E7.3.7.4", {"start": v(8239.13, 2823.23) * mm, "mid": v(8247.92, 2802.01) * mm, "end": v(8269.13, 2793.23) * mm});
            skArc(sketch, "E7.3.7.5", {"start": v(8359.13, 2793.23) * mm, "mid": v(8380.35, 2802.01) * mm, "end": v(8389.13, 2823.23) * mm});
            skLineSegment(sketch, "E7.3.7.6", {"start": v(8389.13, 2913.23) * mm, "end": v(8389.13, 2823.23) * mm});
            skArc(sketch, "E7.3.7.7", {"start": v(8389.13, 2913.23) * mm, "mid": v(8380.35, 2934.44) * mm, "end": v(8359.13, 2943.23) * mm});
            skLineSegment(sketch, "E7.3.8.0", {"start": v(8269.13, 3099.23) * mm, "end": v(8359.13, 3099.23) * mm});
            skArc(sketch, "E7.3.8.1", {"start": v(8269.13, 3099.23) * mm, "mid": v(8247.92, 3090.44) * mm, "end": v(8239.13, 3069.23) * mm});
            skLineSegment(sketch, "E7.3.8.2", {"start": v(8239.13, 3069.23) * mm, "end": v(8239.13, 2979.23) * mm});
            skLineSegment(sketch, "E7.3.8.3", {"start": v(8269.13, 2949.23) * mm, "end": v(8359.13, 2949.23) * mm});
            skArc(sketch, "E7.3.8.4", {"start": v(8239.13, 2979.23) * mm, "mid": v(8247.92, 2958.01) * mm, "end": v(8269.13, 2949.23) * mm});
            skArc(sketch, "E7.3.8.5", {"start": v(8359.13, 2949.23) * mm, "mid": v(8380.35, 2958.01) * mm, "end": v(8389.13, 2979.23) * mm});
            skLineSegment(sketch, "E7.3.8.6", {"start": v(8389.13, 3069.23) * mm, "end": v(8389.13, 2979.23) * mm});
            skArc(sketch, "E7.3.8.7", {"start": v(8389.13, 3069.23) * mm, "mid": v(8380.35, 3090.44) * mm, "end": v(8359.13, 3099.23) * mm});
            skLineSegment(sketch, "E7.3.9.0", {"start": v(8269.13, 3255.23) * mm, "end": v(8359.13, 3255.23) * mm});
            skArc(sketch, "E7.3.9.1", {"start": v(8269.13, 3255.23) * mm, "mid": v(8247.92, 3246.44) * mm, "end": v(8239.13, 3225.23) * mm});
            skLineSegment(sketch, "E7.3.9.2", {"start": v(8239.13, 3225.23) * mm, "end": v(8239.13, 3135.23) * mm});
            skLineSegment(sketch, "E7.3.9.3", {"start": v(8269.13, 3105.23) * mm, "end": v(8359.13, 3105.23) * mm});
            skArc(sketch, "E7.3.9.4", {"start": v(8239.13, 3135.23) * mm, "mid": v(8247.92, 3114.01) * mm, "end": v(8269.13, 3105.23) * mm});
            skArc(sketch, "E7.3.9.5", {"start": v(8359.13, 3105.23) * mm, "mid": v(8380.35, 3114.01) * mm, "end": v(8389.13, 3135.23) * mm});
            skLineSegment(sketch, "E7.3.9.6", {"start": v(8389.13, 3225.23) * mm, "end": v(8389.13, 3135.23) * mm});
            skArc(sketch, "E7.3.9.7", {"start": v(8389.13, 3225.23) * mm, "mid": v(8380.35, 3246.44) * mm, "end": v(8359.13, 3255.23) * mm});
            skLineSegment(sketch, "E7.4.0.0", {"start": v(8424.13, 1851.23) * mm, "end": v(8514.13, 1851.23) * mm});
            skArc(sketch, "E7.4.0.1", {"start": v(8424.13, 1851.23) * mm, "mid": v(8402.92, 1842.44) * mm, "end": v(8394.13, 1821.23) * mm});
            skLineSegment(sketch, "E7.4.0.2", {"start": v(8394.13, 1821.23) * mm, "end": v(8394.13, 1731.23) * mm});
            skLineSegment(sketch, "E7.4.0.3", {"start": v(8424.13, 1701.23) * mm, "end": v(8514.13, 1701.23) * mm});
            skArc(sketch, "E7.4.0.4", {"start": v(8394.13, 1731.23) * mm, "mid": v(8402.92, 1710.01) * mm, "end": v(8424.13, 1701.23) * mm});
            skArc(sketch, "E7.4.0.5", {"start": v(8514.13, 1701.23) * mm, "mid": v(8535.35, 1710.01) * mm, "end": v(8544.13, 1731.23) * mm});
            skLineSegment(sketch, "E7.4.0.6", {"start": v(8544.13, 1821.23) * mm, "end": v(8544.13, 1731.23) * mm});
            skArc(sketch, "E7.4.0.7", {"start": v(8544.13, 1821.23) * mm, "mid": v(8535.35, 1842.44) * mm, "end": v(8514.13, 1851.23) * mm});
            skLineSegment(sketch, "E7.4.1.0", {"start": v(8424.13, 2007.23) * mm, "end": v(8514.13, 2007.23) * mm});
            skArc(sketch, "E7.4.1.1", {"start": v(8424.13, 2007.23) * mm, "mid": v(8402.92, 1998.44) * mm, "end": v(8394.13, 1977.23) * mm});
            skLineSegment(sketch, "E7.4.1.2", {"start": v(8394.13, 1977.23) * mm, "end": v(8394.13, 1887.23) * mm});
            skLineSegment(sketch, "E7.4.1.3", {"start": v(8424.13, 1857.23) * mm, "end": v(8514.13, 1857.23) * mm});
            skArc(sketch, "E7.4.1.4", {"start": v(8394.13, 1887.23) * mm, "mid": v(8402.92, 1866.01) * mm, "end": v(8424.13, 1857.23) * mm});
            skArc(sketch, "E7.4.1.5", {"start": v(8514.13, 1857.23) * mm, "mid": v(8535.35, 1866.01) * mm, "end": v(8544.13, 1887.23) * mm});
            skLineSegment(sketch, "E7.4.1.6", {"start": v(8544.13, 1977.23) * mm, "end": v(8544.13, 1887.23) * mm});
            skArc(sketch, "E7.4.1.7", {"start": v(8544.13, 1977.23) * mm, "mid": v(8535.35, 1998.44) * mm, "end": v(8514.13, 2007.23) * mm});
            skLineSegment(sketch, "E7.4.2.0", {"start": v(8424.13, 2163.23) * mm, "end": v(8514.13, 2163.23) * mm});
            skArc(sketch, "E7.4.2.1", {"start": v(8424.13, 2163.23) * mm, "mid": v(8402.92, 2154.44) * mm, "end": v(8394.13, 2133.23) * mm});
            skLineSegment(sketch, "E7.4.2.2", {"start": v(8394.13, 2133.23) * mm, "end": v(8394.13, 2043.23) * mm});
            skLineSegment(sketch, "E7.4.2.3", {"start": v(8424.13, 2013.23) * mm, "end": v(8514.13, 2013.23) * mm});
            skArc(sketch, "E7.4.2.4", {"start": v(8394.13, 2043.23) * mm, "mid": v(8402.92, 2022.01) * mm, "end": v(8424.13, 2013.23) * mm});
            skArc(sketch, "E7.4.2.5", {"start": v(8514.13, 2013.23) * mm, "mid": v(8535.35, 2022.01) * mm, "end": v(8544.13, 2043.23) * mm});
            skLineSegment(sketch, "E7.4.2.6", {"start": v(8544.13, 2133.23) * mm, "end": v(8544.13, 2043.23) * mm});
            skArc(sketch, "E7.4.2.7", {"start": v(8544.13, 2133.23) * mm, "mid": v(8535.35, 2154.44) * mm, "end": v(8514.13, 2163.23) * mm});
            skLineSegment(sketch, "E7.4.3.0", {"start": v(8424.13, 2319.23) * mm, "end": v(8514.13, 2319.23) * mm});
            skArc(sketch, "E7.4.3.1", {"start": v(8424.13, 2319.23) * mm, "mid": v(8402.92, 2310.44) * mm, "end": v(8394.13, 2289.23) * mm});
            skLineSegment(sketch, "E7.4.3.2", {"start": v(8394.13, 2289.23) * mm, "end": v(8394.13, 2199.23) * mm});
            skLineSegment(sketch, "E7.4.3.3", {"start": v(8424.13, 2169.23) * mm, "end": v(8514.13, 2169.23) * mm});
            skArc(sketch, "E7.4.3.4", {"start": v(8394.13, 2199.23) * mm, "mid": v(8402.92, 2178.01) * mm, "end": v(8424.13, 2169.23) * mm});
            skArc(sketch, "E7.4.3.5", {"start": v(8514.13, 2169.23) * mm, "mid": v(8535.35, 2178.01) * mm, "end": v(8544.13, 2199.23) * mm});
            skLineSegment(sketch, "E7.4.3.6", {"start": v(8544.13, 2289.23) * mm, "end": v(8544.13, 2199.23) * mm});
            skArc(sketch, "E7.4.3.7", {"start": v(8544.13, 2289.23) * mm, "mid": v(8535.35, 2310.44) * mm, "end": v(8514.13, 2319.23) * mm});
            skLineSegment(sketch, "E7.4.4.0", {"start": v(8424.13, 2475.23) * mm, "end": v(8514.13, 2475.23) * mm});
            skArc(sketch, "E7.4.4.1", {"start": v(8424.13, 2475.23) * mm, "mid": v(8402.92, 2466.44) * mm, "end": v(8394.13, 2445.23) * mm});
            skLineSegment(sketch, "E7.4.4.2", {"start": v(8394.13, 2445.23) * mm, "end": v(8394.13, 2355.23) * mm});
            skLineSegment(sketch, "E7.4.4.3", {"start": v(8424.13, 2325.23) * mm, "end": v(8514.13, 2325.23) * mm});
            skArc(sketch, "E7.4.4.4", {"start": v(8394.13, 2355.23) * mm, "mid": v(8402.92, 2334.01) * mm, "end": v(8424.13, 2325.23) * mm});
            skArc(sketch, "E7.4.4.5", {"start": v(8514.13, 2325.23) * mm, "mid": v(8535.35, 2334.01) * mm, "end": v(8544.13, 2355.23) * mm});
            skLineSegment(sketch, "E7.4.4.6", {"start": v(8544.13, 2445.23) * mm, "end": v(8544.13, 2355.23) * mm});
            skArc(sketch, "E7.4.4.7", {"start": v(8544.13, 2445.23) * mm, "mid": v(8535.35, 2466.44) * mm, "end": v(8514.13, 2475.23) * mm});
            skLineSegment(sketch, "E7.4.5.0", {"start": v(8424.13, 2631.23) * mm, "end": v(8514.13, 2631.23) * mm});
            skArc(sketch, "E7.4.5.1", {"start": v(8424.13, 2631.23) * mm, "mid": v(8402.92, 2622.44) * mm, "end": v(8394.13, 2601.23) * mm});
            skLineSegment(sketch, "E7.4.5.2", {"start": v(8394.13, 2601.23) * mm, "end": v(8394.13, 2511.23) * mm});
            skLineSegment(sketch, "E7.4.5.3", {"start": v(8424.13, 2481.23) * mm, "end": v(8514.13, 2481.23) * mm});
            skArc(sketch, "E7.4.5.4", {"start": v(8394.13, 2511.23) * mm, "mid": v(8402.92, 2490.01) * mm, "end": v(8424.13, 2481.23) * mm});
            skArc(sketch, "E7.4.5.5", {"start": v(8514.13, 2481.23) * mm, "mid": v(8535.35, 2490.01) * mm, "end": v(8544.13, 2511.23) * mm});
            skLineSegment(sketch, "E7.4.5.6", {"start": v(8544.13, 2601.23) * mm, "end": v(8544.13, 2511.23) * mm});
            skArc(sketch, "E7.4.5.7", {"start": v(8544.13, 2601.23) * mm, "mid": v(8535.35, 2622.44) * mm, "end": v(8514.13, 2631.23) * mm});
            skLineSegment(sketch, "E7.4.6.0", {"start": v(8424.13, 2787.23) * mm, "end": v(8514.13, 2787.23) * mm});
            skArc(sketch, "E7.4.6.1", {"start": v(8424.13, 2787.23) * mm, "mid": v(8402.92, 2778.44) * mm, "end": v(8394.13, 2757.23) * mm});
            skLineSegment(sketch, "E7.4.6.2", {"start": v(8394.13, 2757.23) * mm, "end": v(8394.13, 2667.23) * mm});
            skLineSegment(sketch, "E7.4.6.3", {"start": v(8424.13, 2637.23) * mm, "end": v(8514.13, 2637.23) * mm});
            skArc(sketch, "E7.4.6.4", {"start": v(8394.13, 2667.23) * mm, "mid": v(8402.92, 2646.01) * mm, "end": v(8424.13, 2637.23) * mm});
            skArc(sketch, "E7.4.6.5", {"start": v(8514.13, 2637.23) * mm, "mid": v(8535.35, 2646.01) * mm, "end": v(8544.13, 2667.23) * mm});
            skLineSegment(sketch, "E7.4.6.6", {"start": v(8544.13, 2757.23) * mm, "end": v(8544.13, 2667.23) * mm});
            skArc(sketch, "E7.4.6.7", {"start": v(8544.13, 2757.23) * mm, "mid": v(8535.35, 2778.44) * mm, "end": v(8514.13, 2787.23) * mm});
            skLineSegment(sketch, "E7.4.7.0", {"start": v(8424.13, 2943.23) * mm, "end": v(8514.13, 2943.23) * mm});
            skArc(sketch, "E7.4.7.1", {"start": v(8424.13, 2943.23) * mm, "mid": v(8402.92, 2934.44) * mm, "end": v(8394.13, 2913.23) * mm});
            skLineSegment(sketch, "E7.4.7.2", {"start": v(8394.13, 2913.23) * mm, "end": v(8394.13, 2823.23) * mm});
            skLineSegment(sketch, "E7.4.7.3", {"start": v(8424.13, 2793.23) * mm, "end": v(8514.13, 2793.23) * mm});
            skArc(sketch, "E7.4.7.4", {"start": v(8394.13, 2823.23) * mm, "mid": v(8402.92, 2802.01) * mm, "end": v(8424.13, 2793.23) * mm});
            skArc(sketch, "E7.4.7.5", {"start": v(8514.13, 2793.23) * mm, "mid": v(8535.35, 2802.01) * mm, "end": v(8544.13, 2823.23) * mm});
            skLineSegment(sketch, "E7.4.7.6", {"start": v(8544.13, 2913.23) * mm, "end": v(8544.13, 2823.23) * mm});
            skArc(sketch, "E7.4.7.7", {"start": v(8544.13, 2913.23) * mm, "mid": v(8535.35, 2934.44) * mm, "end": v(8514.13, 2943.23) * mm});
            skLineSegment(sketch, "E7.4.8.0", {"start": v(8424.13, 3099.23) * mm, "end": v(8514.13, 3099.23) * mm});
            skArc(sketch, "E7.4.8.1", {"start": v(8424.13, 3099.23) * mm, "mid": v(8402.92, 3090.44) * mm, "end": v(8394.13, 3069.23) * mm});
            skLineSegment(sketch, "E7.4.8.2", {"start": v(8394.13, 3069.23) * mm, "end": v(8394.13, 2979.23) * mm});
            skLineSegment(sketch, "E7.4.8.3", {"start": v(8424.13, 2949.23) * mm, "end": v(8514.13, 2949.23) * mm});
            skArc(sketch, "E7.4.8.4", {"start": v(8394.13, 2979.23) * mm, "mid": v(8402.92, 2958.01) * mm, "end": v(8424.13, 2949.23) * mm});
            skArc(sketch, "E7.4.8.5", {"start": v(8514.13, 2949.23) * mm, "mid": v(8535.35, 2958.01) * mm, "end": v(8544.13, 2979.23) * mm});
            skLineSegment(sketch, "E7.4.8.6", {"start": v(8544.13, 3069.23) * mm, "end": v(8544.13, 2979.23) * mm});
            skArc(sketch, "E7.4.8.7", {"start": v(8544.13, 3069.23) * mm, "mid": v(8535.35, 3090.44) * mm, "end": v(8514.13, 3099.23) * mm});
            skLineSegment(sketch, "E7.4.9.0", {"start": v(8424.13, 3255.23) * mm, "end": v(8514.13, 3255.23) * mm});
            skArc(sketch, "E7.4.9.1", {"start": v(8424.13, 3255.23) * mm, "mid": v(8402.92, 3246.44) * mm, "end": v(8394.13, 3225.23) * mm});
            skLineSegment(sketch, "E7.4.9.2", {"start": v(8394.13, 3225.23) * mm, "end": v(8394.13, 3135.23) * mm});
            skLineSegment(sketch, "E7.4.9.3", {"start": v(8424.13, 3105.23) * mm, "end": v(8514.13, 3105.23) * mm});
            skArc(sketch, "E7.4.9.4", {"start": v(8394.13, 3135.23) * mm, "mid": v(8402.92, 3114.01) * mm, "end": v(8424.13, 3105.23) * mm});
            skArc(sketch, "E7.4.9.5", {"start": v(8514.13, 3105.23) * mm, "mid": v(8535.35, 3114.01) * mm, "end": v(8544.13, 3135.23) * mm});
            skLineSegment(sketch, "E7.4.9.6", {"start": v(8544.13, 3225.23) * mm, "end": v(8544.13, 3135.23) * mm});
            skArc(sketch, "E7.4.9.7", {"start": v(8544.13, 3225.23) * mm, "mid": v(8535.35, 3246.44) * mm, "end": v(8514.13, 3255.23) * mm});
            skLineSegment(sketch, "E7.5.0.0", {"start": v(8579.13, 1851.23) * mm, "end": v(8669.13, 1851.23) * mm});
            skArc(sketch, "E7.5.0.1", {"start": v(8579.13, 1851.23) * mm, "mid": v(8557.92, 1842.44) * mm, "end": v(8549.13, 1821.23) * mm});
            skLineSegment(sketch, "E7.5.0.2", {"start": v(8549.13, 1821.23) * mm, "end": v(8549.13, 1731.23) * mm});
            skLineSegment(sketch, "E7.5.0.3", {"start": v(8579.13, 1701.23) * mm, "end": v(8669.13, 1701.23) * mm});
            skArc(sketch, "E7.5.0.4", {"start": v(8549.13, 1731.23) * mm, "mid": v(8557.92, 1710.01) * mm, "end": v(8579.13, 1701.23) * mm});
            skArc(sketch, "E7.5.0.5", {"start": v(8669.13, 1701.23) * mm, "mid": v(8690.35, 1710.01) * mm, "end": v(8699.13, 1731.23) * mm});
            skLineSegment(sketch, "E7.5.0.6", {"start": v(8699.13, 1821.23) * mm, "end": v(8699.13, 1731.23) * mm});
            skArc(sketch, "E7.5.0.7", {"start": v(8699.13, 1821.23) * mm, "mid": v(8690.35, 1842.44) * mm, "end": v(8669.13, 1851.23) * mm});
            skLineSegment(sketch, "E7.5.1.0", {"start": v(8579.13, 2007.23) * mm, "end": v(8669.13, 2007.23) * mm});
            skArc(sketch, "E7.5.1.1", {"start": v(8579.13, 2007.23) * mm, "mid": v(8557.92, 1998.44) * mm, "end": v(8549.13, 1977.23) * mm});
            skLineSegment(sketch, "E7.5.1.2", {"start": v(8549.13, 1977.23) * mm, "end": v(8549.13, 1887.23) * mm});
            skLineSegment(sketch, "E7.5.1.3", {"start": v(8579.13, 1857.23) * mm, "end": v(8669.13, 1857.23) * mm});
            skArc(sketch, "E7.5.1.4", {"start": v(8549.13, 1887.23) * mm, "mid": v(8557.92, 1866.01) * mm, "end": v(8579.13, 1857.23) * mm});
            skArc(sketch, "E7.5.1.5", {"start": v(8669.13, 1857.23) * mm, "mid": v(8690.35, 1866.01) * mm, "end": v(8699.13, 1887.23) * mm});
            skLineSegment(sketch, "E7.5.1.6", {"start": v(8699.13, 1977.23) * mm, "end": v(8699.13, 1887.23) * mm});
            skArc(sketch, "E7.5.1.7", {"start": v(8699.13, 1977.23) * mm, "mid": v(8690.35, 1998.44) * mm, "end": v(8669.13, 2007.23) * mm});
            skLineSegment(sketch, "E7.5.2.0", {"start": v(8579.13, 2163.23) * mm, "end": v(8669.13, 2163.23) * mm});
            skArc(sketch, "E7.5.2.1", {"start": v(8579.13, 2163.23) * mm, "mid": v(8557.92, 2154.44) * mm, "end": v(8549.13, 2133.23) * mm});
            skLineSegment(sketch, "E7.5.2.2", {"start": v(8549.13, 2133.23) * mm, "end": v(8549.13, 2043.23) * mm});
            skLineSegment(sketch, "E7.5.2.3", {"start": v(8579.13, 2013.23) * mm, "end": v(8669.13, 2013.23) * mm});
            skArc(sketch, "E7.5.2.4", {"start": v(8549.13, 2043.23) * mm, "mid": v(8557.92, 2022.01) * mm, "end": v(8579.13, 2013.23) * mm});
            skArc(sketch, "E7.5.2.5", {"start": v(8669.13, 2013.23) * mm, "mid": v(8690.35, 2022.01) * mm, "end": v(8699.13, 2043.23) * mm});
            skLineSegment(sketch, "E7.5.2.6", {"start": v(8699.13, 2133.23) * mm, "end": v(8699.13, 2043.23) * mm});
            skArc(sketch, "E7.5.2.7", {"start": v(8699.13, 2133.23) * mm, "mid": v(8690.35, 2154.44) * mm, "end": v(8669.13, 2163.23) * mm});
            skLineSegment(sketch, "E7.5.3.0", {"start": v(8579.13, 2319.23) * mm, "end": v(8669.13, 2319.23) * mm});
            skArc(sketch, "E7.5.3.1", {"start": v(8579.13, 2319.23) * mm, "mid": v(8557.92, 2310.44) * mm, "end": v(8549.13, 2289.23) * mm});
            skLineSegment(sketch, "E7.5.3.2", {"start": v(8549.13, 2289.23) * mm, "end": v(8549.13, 2199.23) * mm});
            skLineSegment(sketch, "E7.5.3.3", {"start": v(8579.13, 2169.23) * mm, "end": v(8669.13, 2169.23) * mm});
            skArc(sketch, "E7.5.3.4", {"start": v(8549.13, 2199.23) * mm, "mid": v(8557.92, 2178.01) * mm, "end": v(8579.13, 2169.23) * mm});
            skArc(sketch, "E7.5.3.5", {"start": v(8669.13, 2169.23) * mm, "mid": v(8690.35, 2178.01) * mm, "end": v(8699.13, 2199.23) * mm});
            skLineSegment(sketch, "E7.5.3.6", {"start": v(8699.13, 2289.23) * mm, "end": v(8699.13, 2199.23) * mm});
            skArc(sketch, "E7.5.3.7", {"start": v(8699.13, 2289.23) * mm, "mid": v(8690.35, 2310.44) * mm, "end": v(8669.13, 2319.23) * mm});
            skLineSegment(sketch, "E7.5.4.0", {"start": v(8579.13, 2475.23) * mm, "end": v(8669.13, 2475.23) * mm});
            skArc(sketch, "E7.5.4.1", {"start": v(8579.13, 2475.23) * mm, "mid": v(8557.92, 2466.44) * mm, "end": v(8549.13, 2445.23) * mm});
            skLineSegment(sketch, "E7.5.4.2", {"start": v(8549.13, 2445.23) * mm, "end": v(8549.13, 2355.23) * mm});
            skLineSegment(sketch, "E7.5.4.3", {"start": v(8579.13, 2325.23) * mm, "end": v(8669.13, 2325.23) * mm});
            skArc(sketch, "E7.5.4.4", {"start": v(8549.13, 2355.23) * mm, "mid": v(8557.92, 2334.01) * mm, "end": v(8579.13, 2325.23) * mm});
            skArc(sketch, "E7.5.4.5", {"start": v(8669.13, 2325.23) * mm, "mid": v(8690.35, 2334.01) * mm, "end": v(8699.13, 2355.23) * mm});
            skLineSegment(sketch, "E7.5.4.6", {"start": v(8699.13, 2445.23) * mm, "end": v(8699.13, 2355.23) * mm});
            skArc(sketch, "E7.5.4.7", {"start": v(8699.13, 2445.23) * mm, "mid": v(8690.35, 2466.44) * mm, "end": v(8669.13, 2475.23) * mm});
            skLineSegment(sketch, "E7.5.5.0", {"start": v(8579.13, 2631.23) * mm, "end": v(8669.13, 2631.23) * mm});
            skArc(sketch, "E7.5.5.1", {"start": v(8579.13, 2631.23) * mm, "mid": v(8557.92, 2622.44) * mm, "end": v(8549.13, 2601.23) * mm});
            skLineSegment(sketch, "E7.5.5.2", {"start": v(8549.13, 2601.23) * mm, "end": v(8549.13, 2511.23) * mm});
            skLineSegment(sketch, "E7.5.5.3", {"start": v(8579.13, 2481.23) * mm, "end": v(8669.13, 2481.23) * mm});
            skArc(sketch, "E7.5.5.4", {"start": v(8549.13, 2511.23) * mm, "mid": v(8557.92, 2490.01) * mm, "end": v(8579.13, 2481.23) * mm});
            skArc(sketch, "E7.5.5.5", {"start": v(8669.13, 2481.23) * mm, "mid": v(8690.35, 2490.01) * mm, "end": v(8699.13, 2511.23) * mm});
            skLineSegment(sketch, "E7.5.5.6", {"start": v(8699.13, 2601.23) * mm, "end": v(8699.13, 2511.23) * mm});
            skArc(sketch, "E7.5.5.7", {"start": v(8699.13, 2601.23) * mm, "mid": v(8690.35, 2622.44) * mm, "end": v(8669.13, 2631.23) * mm});
            skLineSegment(sketch, "E7.5.6.0", {"start": v(8579.13, 2787.23) * mm, "end": v(8669.13, 2787.23) * mm});
            skArc(sketch, "E7.5.6.1", {"start": v(8579.13, 2787.23) * mm, "mid": v(8557.92, 2778.44) * mm, "end": v(8549.13, 2757.23) * mm});
            skLineSegment(sketch, "E7.5.6.2", {"start": v(8549.13, 2757.23) * mm, "end": v(8549.13, 2667.23) * mm});
            skLineSegment(sketch, "E7.5.6.3", {"start": v(8579.13, 2637.23) * mm, "end": v(8669.13, 2637.23) * mm});
            skArc(sketch, "E7.5.6.4", {"start": v(8549.13, 2667.23) * mm, "mid": v(8557.92, 2646.01) * mm, "end": v(8579.13, 2637.23) * mm});
            skArc(sketch, "E7.5.6.5", {"start": v(8669.13, 2637.23) * mm, "mid": v(8690.35, 2646.01) * mm, "end": v(8699.13, 2667.23) * mm});
            skLineSegment(sketch, "E7.5.6.6", {"start": v(8699.13, 2757.23) * mm, "end": v(8699.13, 2667.23) * mm});
            skArc(sketch, "E7.5.6.7", {"start": v(8699.13, 2757.23) * mm, "mid": v(8690.35, 2778.44) * mm, "end": v(8669.13, 2787.23) * mm});
            skLineSegment(sketch, "E7.5.7.0", {"start": v(8579.13, 2943.23) * mm, "end": v(8669.13, 2943.23) * mm});
            skArc(sketch, "E7.5.7.1", {"start": v(8579.13, 2943.23) * mm, "mid": v(8557.92, 2934.44) * mm, "end": v(8549.13, 2913.23) * mm});
            skLineSegment(sketch, "E7.5.7.2", {"start": v(8549.13, 2913.23) * mm, "end": v(8549.13, 2823.23) * mm});
            skLineSegment(sketch, "E7.5.7.3", {"start": v(8579.13, 2793.23) * mm, "end": v(8669.13, 2793.23) * mm});
            skArc(sketch, "E7.5.7.4", {"start": v(8549.13, 2823.23) * mm, "mid": v(8557.92, 2802.01) * mm, "end": v(8579.13, 2793.23) * mm});
            skArc(sketch, "E7.5.7.5", {"start": v(8669.13, 2793.23) * mm, "mid": v(8690.35, 2802.01) * mm, "end": v(8699.13, 2823.23) * mm});
            skLineSegment(sketch, "E7.5.7.6", {"start": v(8699.13, 2913.23) * mm, "end": v(8699.13, 2823.23) * mm});
            skArc(sketch, "E7.5.7.7", {"start": v(8699.13, 2913.23) * mm, "mid": v(8690.35, 2934.44) * mm, "end": v(8669.13, 2943.23) * mm});
            skLineSegment(sketch, "E7.5.8.0", {"start": v(8579.13, 3099.23) * mm, "end": v(8669.13, 3099.23) * mm});
            skArc(sketch, "E7.5.8.1", {"start": v(8579.13, 3099.23) * mm, "mid": v(8557.92, 3090.44) * mm, "end": v(8549.13, 3069.23) * mm});
            skLineSegment(sketch, "E7.5.8.2", {"start": v(8549.13, 3069.23) * mm, "end": v(8549.13, 2979.23) * mm});
            skLineSegment(sketch, "E7.5.8.3", {"start": v(8579.13, 2949.23) * mm, "end": v(8669.13, 2949.23) * mm});
            skArc(sketch, "E7.5.8.4", {"start": v(8549.13, 2979.23) * mm, "mid": v(8557.92, 2958.01) * mm, "end": v(8579.13, 2949.23) * mm});
            skArc(sketch, "E7.5.8.5", {"start": v(8669.13, 2949.23) * mm, "mid": v(8690.35, 2958.01) * mm, "end": v(8699.13, 2979.23) * mm});
            skLineSegment(sketch, "E7.5.8.6", {"start": v(8699.13, 3069.23) * mm, "end": v(8699.13, 2979.23) * mm});
            skArc(sketch, "E7.5.8.7", {"start": v(8699.13, 3069.23) * mm, "mid": v(8690.35, 3090.44) * mm, "end": v(8669.13, 3099.23) * mm});
            skLineSegment(sketch, "E7.5.9.0", {"start": v(8579.13, 3255.23) * mm, "end": v(8669.13, 3255.23) * mm});
            skArc(sketch, "E7.5.9.1", {"start": v(8579.13, 3255.23) * mm, "mid": v(8557.92, 3246.44) * mm, "end": v(8549.13, 3225.23) * mm});
            skLineSegment(sketch, "E7.5.9.2", {"start": v(8549.13, 3225.23) * mm, "end": v(8549.13, 3135.23) * mm});
            skLineSegment(sketch, "E7.5.9.3", {"start": v(8579.13, 3105.23) * mm, "end": v(8669.13, 3105.23) * mm});
            skArc(sketch, "E7.5.9.4", {"start": v(8549.13, 3135.23) * mm, "mid": v(8557.92, 3114.01) * mm, "end": v(8579.13, 3105.23) * mm});
            skArc(sketch, "E7.5.9.5", {"start": v(8669.13, 3105.23) * mm, "mid": v(8690.35, 3114.01) * mm, "end": v(8699.13, 3135.23) * mm});
            skLineSegment(sketch, "E7.5.9.6", {"start": v(8699.13, 3225.23) * mm, "end": v(8699.13, 3135.23) * mm});
            skArc(sketch, "E7.5.9.7", {"start": v(8699.13, 3225.23) * mm, "mid": v(8690.35, 3246.44) * mm, "end": v(8669.13, 3255.23) * mm});
            skLineSegment(sketch, "E7.direction1", {"start": v(7804.13, 1701.23) * mm, "end": v(7959.13, 1701.23) * mm, "construction": true});
            skLineSegment(sketch, "E7.direction2", {"start": v(7804.13, 1701.23) * mm, "end": v(7804.13, 1857.23) * mm, "construction": true});
            skSolve(sketch);
        }
        {
            var Q0;
            Q0=makeQuery(id+"F0.imprint","IMPRINT",FACE,{"disambiguationData":[TD([[makeQuery(id+"F0.imprint","IMPRINT",EDGE,{"derivedFrom":sQuery(id+"F0.wireOp",EDGE,"E0.bottom")}),-1.0]])]});
            extrude(context, id + "F3", {"entities" : qUnion([Q0]), "depth" : 150 * mm, "offsetDistance" : 25 * mm});
        }
        {
            var Q0;
            Q0=makeQuery(id+"F2.imprint","IMPRINT",FACE,{"disambiguationData":[TD([[makeQuery(id+"F2.imprint","IMPRINT",EDGE,{"derivedFrom":sQuery(id+"F2.wireOp",EDGE,"E7.5.9.0")}),-1.0]])]});
            var Q1;
            Q1=makeQuery(id+"F2.imprint","IMPRINT",FACE,{"disambiguationData":[TD([[makeQuery(id+"F2.imprint","IMPRINT",EDGE,{"derivedFrom":sQuery(id+"F2.wireOp",EDGE,"E7.3.8.0")}),-1.0]])]});
            var Q2;
            Q2=makeQuery(id+"F2.imprint","IMPRINT",FACE,{"disambiguationData":[TD([[makeQuery(id+"F2.imprint","IMPRINT",EDGE,{"derivedFrom":sQuery(id+"F2.wireOp",EDGE,"E7.4.8.0")}),-1.0]])]});
            var Q3;
            Q3=makeQuery(id+"F2.imprint","IMPRINT",FACE,{"disambiguationData":[TD([[makeQuery(id+"F2.imprint","IMPRINT",EDGE,{"derivedFrom":sQuery(id+"F2.wireOp",EDGE,"E7.5.7.0")}),-1.0]])]});
            var Q4;
            Q4=makeQuery(id+"F2.imprint","IMPRINT",FACE,{"disambiguationData":[TD([[makeQuery(id+"F2.imprint","IMPRINT",EDGE,{"derivedFrom":sQuery(id+"F2.wireOp",EDGE,"E7.0.4.0")}),-1.0]])]});
            var Q5;
            Q5=makeQuery(id+"F2.imprint","IMPRINT",FACE,{"disambiguationData":[TD([[makeQuery(id+"F2.imprint","IMPRINT",EDGE,{"derivedFrom":sQuery(id+"F2.wireOp",EDGE,"E7.0.3.0")}),-1.0]])]});
            var Q6;
            Q6=makeQuery(id+"F2.imprint","IMPRINT",FACE,{"disambiguationData":[TD([[makeQuery(id+"F2.imprint","IMPRINT",EDGE,{"derivedFrom":sQuery(id+"F2.wireOp",EDGE,"E7.0.2.0")}),-1.0]])]});
            var Q7;
            Q7=makeQuery(id+"F2.imprint","IMPRINT",FACE,{"disambiguationData":[TD([[makeQuery(id+"F2.imprint","IMPRINT",EDGE,{"derivedFrom":sQuery(id+"F2.wireOp",EDGE,"E7.1.2.0")}),-1.0]])]});
            var Q8;
            Q8=makeQuery(id+"F2.imprint","IMPRINT",FACE,{"disambiguationData":[TD([[makeQuery(id+"F2.imprint","IMPRINT",EDGE,{"derivedFrom":sQuery(id+"F2.wireOp",EDGE,"E7.1.1.0")}),-1.0]])]});
            var Q9;
            Q9=makeQuery(id+"F2.imprint","IMPRINT",FACE,{"disambiguationData":[TD([[makeQuery(id+"F2.imprint","IMPRINT",EDGE,{"derivedFrom":sQuery(id+"F2.wireOp",EDGE,"E7.0.1.0")}),-1.0]])]});
            var Q10;
            Q10=makeQuery(id+"F2.imprint","IMPRINT",FACE,{"disambiguationData":[TD([[makeQuery(id+"F2.imprint","IMPRINT",EDGE,{"derivedFrom":sQuery(id+"F2.wireOp",EDGE,"E2.bottom")}),-1.0]])]});
            var Q11;
            Q11=makeQuery(id+"F2.imprint","IMPRINT",FACE,{"disambiguationData":[TD([[makeQuery(id+"F2.imprint","IMPRINT",EDGE,{"derivedFrom":sQuery(id+"F2.wireOp",EDGE,"E7.1.0.0")}),-1.0]])]});
            var Q12;
            Q12=makeQuery(id+"F2.imprint","IMPRINT",FACE,{"disambiguationData":[TD([[makeQuery(id+"F2.imprint","IMPRINT",EDGE,{"derivedFrom":sQuery(id+"F2.wireOp",EDGE,"E7.2.0.0")}),-1.0]])]});
            var Q13;
            Q13=makeQuery(id+"F2.imprint","IMPRINT",FACE,{"disambiguationData":[TD([[makeQuery(id+"F2.imprint","IMPRINT",EDGE,{"derivedFrom":sQuery(id+"F2.wireOp",EDGE,"E7.3.0.0")}),-1.0]])]});
            var Q14;
            Q14=makeQuery(id+"F2.imprint","IMPRINT",FACE,{"disambiguationData":[TD([[makeQuery(id+"F2.imprint","IMPRINT",EDGE,{"derivedFrom":sQuery(id+"F2.wireOp",EDGE,"E7.4.0.0")}),-1.0]])]});
            var Q15;
            Q15=makeQuery(id+"F2.imprint","IMPRINT",FACE,{"disambiguationData":[TD([[makeQuery(id+"F2.imprint","IMPRINT",EDGE,{"derivedFrom":sQuery(id+"F2.wireOp",EDGE,"E7.5.0.0")}),-1.0]])]});
            var Q16;
            Q16=makeQuery(id+"F2.imprint","IMPRINT",FACE,{"disambiguationData":[TD([[makeQuery(id+"F2.imprint","IMPRINT",EDGE,{"derivedFrom":sQuery(id+"F2.wireOp",EDGE,"E7.5.1.0")}),-1.0]])]});
            var Q17;
            Q17=makeQuery(id+"F2.imprint","IMPRINT",FACE,{"disambiguationData":[TD([[makeQuery(id+"F2.imprint","IMPRINT",EDGE,{"derivedFrom":sQuery(id+"F2.wireOp",EDGE,"E7.4.1.0")}),-1.0]])]});
            var Q18;
            Q18=makeQuery(id+"F2.imprint","IMPRINT",FACE,{"disambiguationData":[TD([[makeQuery(id+"F2.imprint","IMPRINT",EDGE,{"derivedFrom":sQuery(id+"F2.wireOp",EDGE,"E7.3.1.0")}),-1.0]])]});
            var Q19;
            Q19=makeQuery(id+"F2.imprint","IMPRINT",FACE,{"disambiguationData":[TD([[makeQuery(id+"F2.imprint","IMPRINT",EDGE,{"derivedFrom":sQuery(id+"F2.wireOp",EDGE,"E7.2.1.0")}),-1.0]])]});
            var Q20;
            Q20=makeQuery(id+"F2.imprint","IMPRINT",FACE,{"disambiguationData":[TD([[makeQuery(id+"F2.imprint","IMPRINT",EDGE,{"derivedFrom":sQuery(id+"F2.wireOp",EDGE,"E7.2.2.0")}),-1.0]])]});
            var Q21;
            Q21=makeQuery(id+"F2.imprint","IMPRINT",FACE,{"disambiguationData":[TD([[makeQuery(id+"F2.imprint","IMPRINT",EDGE,{"derivedFrom":sQuery(id+"F2.wireOp",EDGE,"E7.3.2.0")}),-1.0]])]});
            var Q22;
            Q22=makeQuery(id+"F2.imprint","IMPRINT",FACE,{"disambiguationData":[TD([[makeQuery(id+"F2.imprint","IMPRINT",EDGE,{"derivedFrom":sQuery(id+"F2.wireOp",EDGE,"E7.4.2.0")}),-1.0]])]});
            var Q23;
            Q23=makeQuery(id+"F2.imprint","IMPRINT",FACE,{"disambiguationData":[TD([[makeQuery(id+"F2.imprint","IMPRINT",EDGE,{"derivedFrom":sQuery(id+"F2.wireOp",EDGE,"E7.5.2.0")}),-1.0]])]});
            var Q24;
            Q24=makeQuery(id+"F2.imprint","IMPRINT",FACE,{"disambiguationData":[TD([[makeQuery(id+"F2.imprint","IMPRINT",EDGE,{"derivedFrom":sQuery(id+"F2.wireOp",EDGE,"E7.5.3.0")}),-1.0]])]});
            var Q25;
            Q25=makeQuery(id+"F2.imprint","IMPRINT",FACE,{"disambiguationData":[TD([[makeQuery(id+"F2.imprint","IMPRINT",EDGE,{"derivedFrom":sQuery(id+"F2.wireOp",EDGE,"E7.4.3.0")}),-1.0]])]});
            var Q26;
            Q26=makeQuery(id+"F2.imprint","IMPRINT",FACE,{"disambiguationData":[TD([[makeQuery(id+"F2.imprint","IMPRINT",EDGE,{"derivedFrom":sQuery(id+"F2.wireOp",EDGE,"E7.3.3.0")}),-1.0]])]});
            var Q27;
            Q27=makeQuery(id+"F2.imprint","IMPRINT",FACE,{"disambiguationData":[TD([[makeQuery(id+"F2.imprint","IMPRINT",EDGE,{"derivedFrom":sQuery(id+"F2.wireOp",EDGE,"E7.2.3.0")}),-1.0]])]});
            var Q28;
            Q28=makeQuery(id+"F2.imprint","IMPRINT",FACE,{"disambiguationData":[TD([[makeQuery(id+"F2.imprint","IMPRINT",EDGE,{"derivedFrom":sQuery(id+"F2.wireOp",EDGE,"E7.1.3.0")}),-1.0]])]});
            var Q29;
            Q29=makeQuery(id+"F2.imprint","IMPRINT",FACE,{"disambiguationData":[TD([[makeQuery(id+"F2.imprint","IMPRINT",EDGE,{"derivedFrom":sQuery(id+"F2.wireOp",EDGE,"E7.1.4.0")}),-1.0]])]});
            var Q30;
            Q30=makeQuery(id+"F2.imprint","IMPRINT",FACE,{"disambiguationData":[TD([[makeQuery(id+"F2.imprint","IMPRINT",EDGE,{"derivedFrom":sQuery(id+"F2.wireOp",EDGE,"E7.2.4.0")}),-1.0]])]});
            var Q31;
            Q31=makeQuery(id+"F2.imprint","IMPRINT",FACE,{"disambiguationData":[TD([[makeQuery(id+"F2.imprint","IMPRINT",EDGE,{"derivedFrom":sQuery(id+"F2.wireOp",EDGE,"E7.3.4.0")}),-1.0]])]});
            var Q32;
            Q32=makeQuery(id+"F2.imprint","IMPRINT",FACE,{"disambiguationData":[TD([[makeQuery(id+"F2.imprint","IMPRINT",EDGE,{"derivedFrom":sQuery(id+"F2.wireOp",EDGE,"E7.4.4.0")}),-1.0]])]});
            var Q33;
            Q33=makeQuery(id+"F2.imprint","IMPRINT",FACE,{"disambiguationData":[TD([[makeQuery(id+"F2.imprint","IMPRINT",EDGE,{"derivedFrom":sQuery(id+"F2.wireOp",EDGE,"E7.5.4.0")}),-1.0]])]});
            var Q34;
            Q34=makeQuery(id+"F2.imprint","IMPRINT",FACE,{"disambiguationData":[TD([[makeQuery(id+"F2.imprint","IMPRINT",EDGE,{"derivedFrom":sQuery(id+"F2.wireOp",EDGE,"E7.5.5.0")}),-1.0]])]});
            var Q35;
            Q35=makeQuery(id+"F2.imprint","IMPRINT",FACE,{"disambiguationData":[TD([[makeQuery(id+"F2.imprint","IMPRINT",EDGE,{"derivedFrom":sQuery(id+"F2.wireOp",EDGE,"E7.4.5.0")}),-1.0]])]});
            var Q36;
            Q36=makeQuery(id+"F2.imprint","IMPRINT",FACE,{"disambiguationData":[TD([[makeQuery(id+"F2.imprint","IMPRINT",EDGE,{"derivedFrom":sQuery(id+"F2.wireOp",EDGE,"E7.3.5.0")}),-1.0]])]});
            var Q37;
            Q37=makeQuery(id+"F2.imprint","IMPRINT",FACE,{"disambiguationData":[TD([[makeQuery(id+"F2.imprint","IMPRINT",EDGE,{"derivedFrom":sQuery(id+"F2.wireOp",EDGE,"E7.2.5.0")}),-1.0]])]});
            var Q38;
            Q38=makeQuery(id+"F2.imprint","IMPRINT",FACE,{"disambiguationData":[TD([[makeQuery(id+"F2.imprint","IMPRINT",EDGE,{"derivedFrom":sQuery(id+"F2.wireOp",EDGE,"E7.1.5.0")}),-1.0]])]});
            var Q39;
            Q39=makeQuery(id+"F2.imprint","IMPRINT",FACE,{"disambiguationData":[TD([[makeQuery(id+"F2.imprint","IMPRINT",EDGE,{"derivedFrom":sQuery(id+"F2.wireOp",EDGE,"E7.0.5.0")}),-1.0]])]});
            var Q40;
            Q40=makeQuery(id+"F2.imprint","IMPRINT",FACE,{"disambiguationData":[TD([[makeQuery(id+"F2.imprint","IMPRINT",EDGE,{"derivedFrom":sQuery(id+"F2.wireOp",EDGE,"E7.0.6.0")}),-1.0]])]});
            var Q41;
            Q41=makeQuery(id+"F2.imprint","IMPRINT",FACE,{"disambiguationData":[TD([[makeQuery(id+"F2.imprint","IMPRINT",EDGE,{"derivedFrom":sQuery(id+"F2.wireOp",EDGE,"E7.2.6.0")}),-1.0]])]});
            var Q42;
            Q42=makeQuery(id+"F2.imprint","IMPRINT",FACE,{"disambiguationData":[TD([[makeQuery(id+"F2.imprint","IMPRINT",EDGE,{"derivedFrom":sQuery(id+"F2.wireOp",EDGE,"E7.5.6.0")}),-1.0]])]});
            var Q43;
            Q43=makeQuery(id+"F2.imprint","IMPRINT",FACE,{"disambiguationData":[TD([[makeQuery(id+"F2.imprint","IMPRINT",EDGE,{"derivedFrom":sQuery(id+"F2.wireOp",EDGE,"E7.0.8.0")}),-1.0]])]});
            var Q44;
            Q44=makeQuery(id+"F2.imprint","IMPRINT",FACE,{"disambiguationData":[TD([[makeQuery(id+"F2.imprint","IMPRINT",EDGE,{"derivedFrom":sQuery(id+"F2.wireOp",EDGE,"E7.4.7.0")}),-1.0]])]});
            var Q45;
            Q45=makeQuery(id+"F2.imprint","IMPRINT",FACE,{"disambiguationData":[TD([[makeQuery(id+"F2.imprint","IMPRINT",EDGE,{"derivedFrom":sQuery(id+"F2.wireOp",EDGE,"E7.3.7.0")}),-1.0]])]});
            var Q46;
            Q46=makeQuery(id+"F2.imprint","IMPRINT",FACE,{"disambiguationData":[TD([[makeQuery(id+"F2.imprint","IMPRINT",EDGE,{"derivedFrom":sQuery(id+"F2.wireOp",EDGE,"E7.2.7.0")}),-1.0]])]});
            var Q47;
            Q47=makeQuery(id+"F2.imprint","IMPRINT",FACE,{"disambiguationData":[TD([[makeQuery(id+"F2.imprint","IMPRINT",EDGE,{"derivedFrom":sQuery(id+"F2.wireOp",EDGE,"E7.1.7.0")}),-1.0]])]});
            var Q48;
            Q48=makeQuery(id+"F2.imprint","IMPRINT",FACE,{"disambiguationData":[TD([[makeQuery(id+"F2.imprint","IMPRINT",EDGE,{"derivedFrom":sQuery(id+"F2.wireOp",EDGE,"E7.1.6.0")}),-1.0]])]});
            var Q49;
            Q49=makeQuery(id+"F2.imprint","IMPRINT",FACE,{"disambiguationData":[TD([[makeQuery(id+"F2.imprint","IMPRINT",EDGE,{"derivedFrom":sQuery(id+"F2.wireOp",EDGE,"E7.3.6.0")}),-1.0]])]});
            var Q50;
            Q50=makeQuery(id+"F2.imprint","IMPRINT",FACE,{"disambiguationData":[TD([[makeQuery(id+"F2.imprint","IMPRINT",EDGE,{"derivedFrom":sQuery(id+"F2.wireOp",EDGE,"E7.4.6.0")}),-1.0]])]});
            var Q51;
            Q51=makeQuery(id+"F2.imprint","IMPRINT",FACE,{"disambiguationData":[TD([[makeQuery(id+"F2.imprint","IMPRINT",EDGE,{"derivedFrom":sQuery(id+"F2.wireOp",EDGE,"E7.0.7.0")}),-1.0]])]});
            var Q52;
            Q52=makeQuery(id+"F2.imprint","IMPRINT",FACE,{"disambiguationData":[TD([[makeQuery(id+"F2.imprint","IMPRINT",EDGE,{"derivedFrom":sQuery(id+"F2.wireOp",EDGE,"E7.1.8.0")}),-1.0]])]});
            var Q53;
            Q53=makeQuery(id+"F2.imprint","IMPRINT",FACE,{"disambiguationData":[TD([[makeQuery(id+"F2.imprint","IMPRINT",EDGE,{"derivedFrom":sQuery(id+"F2.wireOp",EDGE,"E7.2.8.0")}),-1.0]])]});
            var Q54;
            Q54=makeQuery(id+"F2.imprint","IMPRINT",FACE,{"disambiguationData":[TD([[makeQuery(id+"F2.imprint","IMPRINT",EDGE,{"derivedFrom":sQuery(id+"F2.wireOp",EDGE,"E7.5.8.0")}),-1.0]])]});
            var Q55;
            Q55=makeQuery(id+"F2.imprint","IMPRINT",FACE,{"disambiguationData":[TD([[makeQuery(id+"F2.imprint","IMPRINT",EDGE,{"derivedFrom":sQuery(id+"F2.wireOp",EDGE,"E7.0.9.0")}),-1.0]])]});
            var Q56;
            Q56=makeQuery(id+"F2.imprint","IMPRINT",FACE,{"disambiguationData":[TD([[makeQuery(id+"F2.imprint","IMPRINT",EDGE,{"derivedFrom":sQuery(id+"F2.wireOp",EDGE,"E7.1.9.0")}),-1.0]])]});
            var Q57;
            Q57=makeQuery(id+"F2.imprint","IMPRINT",FACE,{"disambiguationData":[TD([[makeQuery(id+"F2.imprint","IMPRINT",EDGE,{"derivedFrom":sQuery(id+"F2.wireOp",EDGE,"E7.2.9.0")}),-1.0]])]});
            var Q58;
            Q58=makeQuery(id+"F2.imprint","IMPRINT",FACE,{"disambiguationData":[TD([[makeQuery(id+"F2.imprint","IMPRINT",EDGE,{"derivedFrom":sQuery(id+"F2.wireOp",EDGE,"E7.3.9.0")}),-1.0]])]});
            var Q59;
            Q59=makeQuery(id+"F2.imprint","IMPRINT",FACE,{"disambiguationData":[TD([[makeQuery(id+"F2.imprint","IMPRINT",EDGE,{"derivedFrom":sQuery(id+"F2.wireOp",EDGE,"E7.4.9.0")}),-1.0]])]});
            extrude(context, id + "F4", {"entities" : qUnion([Q0, Q1, Q2, Q3, Q4, Q5, Q6, Q7, Q8, Q9, Q10, Q11, Q12, Q13, Q14, Q15, Q16, Q17, Q18, Q19, Q20, Q21, Q22, Q23, Q24, Q25, Q26, Q27, Q28, Q29, Q30, Q31, Q32, Q33, Q34, Q35, Q36, Q37, Q38, Q39, Q40, Q41, Q42, Q43, Q44, Q45, Q46, Q47, Q48, Q49, Q50, Q51, Q52, Q53, Q54, Q55, Q56, Q57, Q58, Q59]), "depth" : 2 * mm, "offsetDistance" : 25 * mm});
        }
        {
            var Q0;
            Q0=makeQuery(id+"F1.imprint","IMPRINT",FACE,{"disambiguationData":[TD([[makeQuery(id+"F1.imprint","IMPRINT",EDGE,{"derivedFrom":sQuery(id+"F1.wireOp",EDGE,"E1.bottom")}),-1.0]])]});
            extrude(context, id + "F5", {"entities" : qUnion([Q0]), "depth" : 0.1 * mm, "offsetDistance" : 25 * mm});
        }
    });
